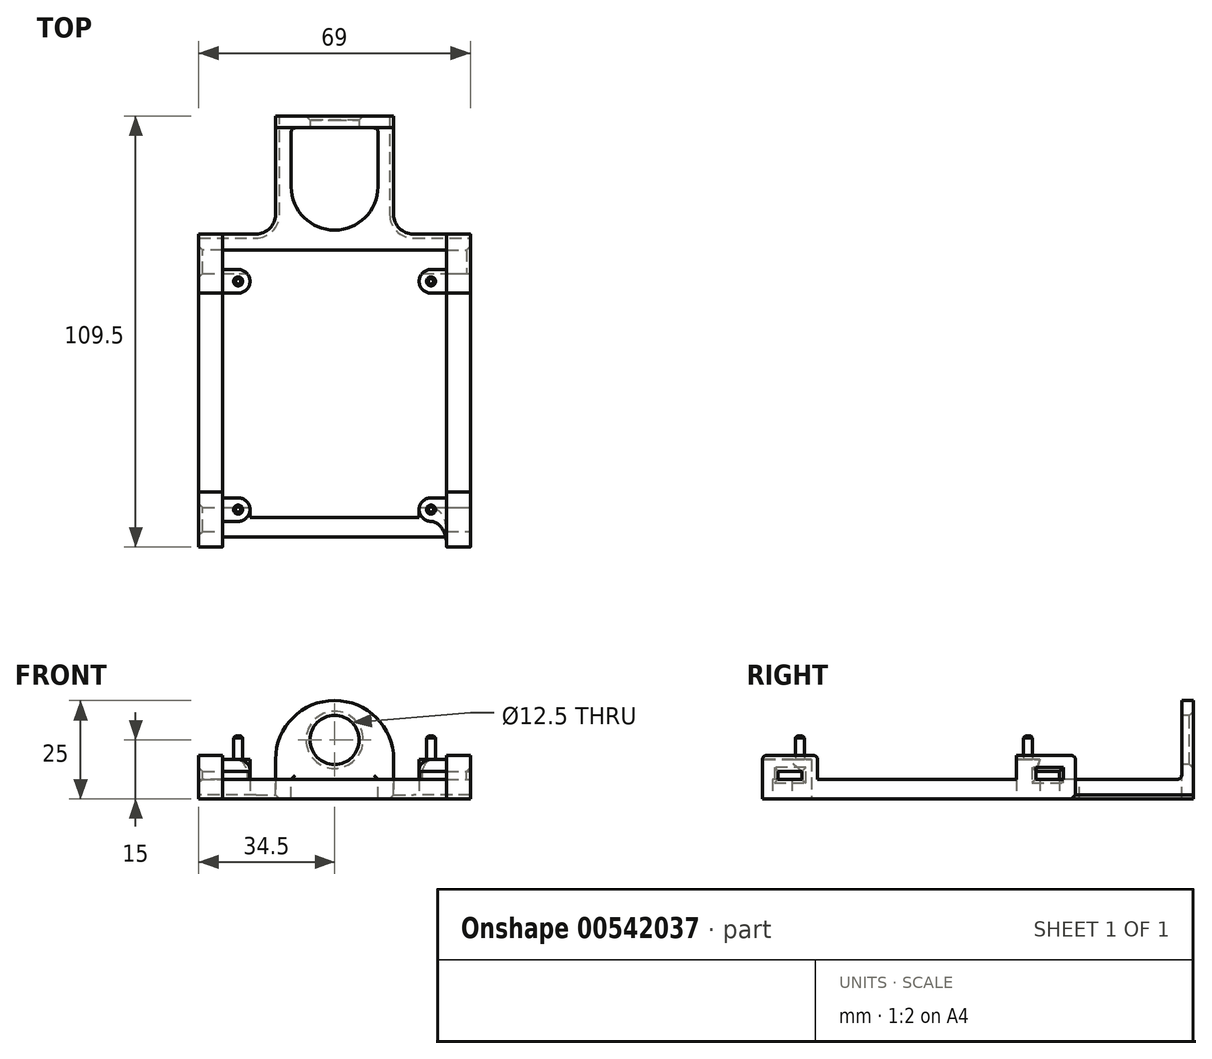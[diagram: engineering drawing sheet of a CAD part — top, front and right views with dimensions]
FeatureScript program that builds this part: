
annotation { "Feature Type Name" : "Feature", "Feature Type Description" : "" }
export const myFeature = defineFeature(function(context is Context, id is Id, definition is map)
    precondition{}
    {
        {
            var Q0;
            Q0=qCreatedBy(makeId("Top.planeOp"),FACE);
            var sketch = newSketch(context, id + "F0", { "sketchPlane" : qUnion([Q0])});
            skCircle(sketch, "E0", {"center": v(0, 58) * mm, "radius": 3 * mm, "construction": true});
            skCircle(sketch, "E1", {"center": v(49, 58) * mm, "radius": 3 * mm, "construction": true});
            skCircle(sketch, "E2", {"center": v(0, 0) * mm, "radius": 3 * mm, "construction": true});
            skCircle(sketch, "E3", {"center": v(49, 0) * mm, "radius": 3 * mm, "construction": true});
            skLineSegment(sketch, "E4", {"start": v(0, 58) * mm, "end": v(0, 0) * mm, "construction": true});
            skLineSegment(sketch, "E5", {"start": v(49, 0) * mm, "end": v(49, 58) * mm, "construction": true});
            skLineSegment(sketch, "E6", {"start": v(0, 58) * mm, "end": v(49, 58) * mm, "construction": true});
            skLineSegment(sketch, "E7", {"start": v(49, 0) * mm, "end": v(0, 0) * mm, "construction": true});
            skLineSegment(sketch, "E8", {"start": v(53, 87) * mm, "end": v(59, 87) * mm});
            skLineSegment(sketch, "E9", {"start": v(59, 87) * mm, "end": v(59, -8) * mm});
            skLineSegment(sketch, "E10", {"start": v(59, -8) * mm, "end": v(-10, -8) * mm});
            skLineSegment(sketch, "E11", {"start": v(-10, -8) * mm, "end": v(-10, 87) * mm});
            skLineSegment(sketch, "E12", {"start": v(-10, 87) * mm, "end": v(-4, 87) * mm});
            skLineSegment(sketch, "E13", {"start": v(-4, -2) * mm, "end": v(53, -2) * mm});
            skLineSegment(sketch, "E14", {"start": v(-4, 61) * mm, "end": v(0, 61) * mm});
            skLineSegment(sketch, "E15", {"start": v(0, 55) * mm, "end": v(-4, 55) * mm});
            skLineSegment(sketch, "E16", {"start": v(-4, 87) * mm, "end": v(-4, 61) * mm});
            skLineSegment(sketch, "E17", {"start": v(-4, 55) * mm, "end": v(-4, -2) * mm});
            skLineSegment(sketch, "E18", {"start": v(49, 55) * mm, "end": v(53, 55) * mm});
            skArc(sketch, "E19", {"start": v(49, 61) * mm, "mid": v(46, 58) * mm, "end": v(49, 55) * mm});
            skLineSegment(sketch, "E20", {"start": v(53, 87) * mm, "end": v(53, 61) * mm});
            skLineSegment(sketch, "E21", {"start": v(53, 55) * mm, "end": v(53, -2) * mm});
            skLineSegment(sketch, "E22", {"start": v(49, 61) * mm, "end": v(53, 61) * mm});
            skArc(sketch, "E23", {"start": v(0, 55) * mm, "mid": v(3, 58) * mm, "end": v(0, 61) * mm});
            skSolve(sketch);
        }
        {
            var Q0;
            Q0=qSketchRegion(id+"F0",true);
            extrude(context, id + "F1", {"entities" : qUnion([Q0]), "depth" : 5 * mm, "offsetDistance" : 25 * mm});
        }
        {
            var Q0;
            Q0=makeQuery(id+"F0.imprint","IMPRINT",FACE,{"disambiguationData":[TD([[makeQuery(id+"F0.imprint","IMPRINT",EDGE,{"derivedFrom":sQuery(id+"F0.wireOp",EDGE,"E8")}),-1.0]])]});
            var sketch = newSketch(context, id + "F2", { "sketchPlane" : qUnion([Q0])});
            skCircle(sketch, "E24.0", {"center": v(0, 0) * mm, "radius": 3 * mm});
            skCircle(sketch, "E24.1", {"center": v(49, 0) * mm, "radius": 3 * mm});
            skCircle(sketch, "E24.2", {"center": v(49, 58) * mm, "radius": 3 * mm});
            skCircle(sketch, "E24.3", {"center": v(0, 58) * mm, "radius": 3 * mm});
            skSolve(sketch);
        }
        {
            var Q0;
            {var subQ0=sQuery(id+"F2.wireOp",EDGE,"E24.0");var subQ1=makeQuery(id+"F0.imprint","IMPRINT",EDGE,{"derivedFrom":sQuery(id+"F0.wireOp",EDGE,"z0m1eTGF-zZ5E-Jgir-b5gq-jupZHO1aANQM")});var subQ2=makeQuery(id+"F2.imprint","INTERSECT",VERTEX,{"disambiguationData":[OD(0.0)],"derivedFrom":[subQ1,subQ0]});Q0=makeQuery(id+"F2.imprint","IMPRINT",FACE,{"disambiguationData":[TD([[makeQuery(id+"F2.imprint","IMPRINT",EDGE,{"disambiguationData":[TD([[subQ2,-1.0]])],"derivedFrom":subQ0}),1.0]])]});}
            var Q1;
            {var subQ0=sQuery(id+"F2.wireOp",EDGE,"E24.1");var subQ1=makeQuery(id+"F0.imprint","IMPRINT",EDGE,{"derivedFrom":sQuery(id+"F0.wireOp",EDGE,"CqdVWxwD-0q4v-9Kh3-cIFh-dPhWwpQpFwKd")});var subQ2=makeQuery(id+"F2.imprint","INTERSECT",VERTEX,{"disambiguationData":[OD(0.0)],"derivedFrom":[subQ1,subQ0]});Q1=makeQuery(id+"F2.imprint","IMPRINT",FACE,{"disambiguationData":[TD([[makeQuery(id+"F2.imprint","IMPRINT",EDGE,{"disambiguationData":[TD([[subQ2,1.0]])],"derivedFrom":subQ0}),1.0]])]});}
            var Q2;
            {var subQ0=sQuery(id+"F2.wireOp",EDGE,"E24.2");var subQ1=makeQuery(id+"F0.imprint","IMPRINT",EDGE,{"derivedFrom":sQuery(id+"F0.wireOp",EDGE,"CqdVWxwD-0q4v-9Kh3-cIFh-dPhWwpQpFwKd")});var subQ2=makeQuery(id+"F2.imprint","INTERSECT",VERTEX,{"disambiguationData":[OD(0.0)],"derivedFrom":[subQ1,subQ0]});Q2=makeQuery(id+"F2.imprint","IMPRINT",FACE,{"disambiguationData":[TD([[makeQuery(id+"F2.imprint","IMPRINT",EDGE,{"disambiguationData":[TD([[subQ2,-1.0]])],"derivedFrom":subQ0}),1.0]])]});}
            var Q3;
            {var subQ0=sQuery(id+"F2.wireOp",EDGE,"E24.3");var subQ1=makeQuery(id+"F0.imprint","IMPRINT",EDGE,{"derivedFrom":sQuery(id+"F0.wireOp",EDGE,"z0m1eTGF-zZ5E-Jgir-b5gq-jupZHO1aANQM")});var subQ2=makeQuery(id+"F2.imprint","INTERSECT",VERTEX,{"disambiguationData":[OD(0.0)],"derivedFrom":[subQ1,subQ0]});Q3=makeQuery(id+"F2.imprint","IMPRINT",FACE,{"disambiguationData":[TD([[makeQuery(id+"F2.imprint","IMPRINT",EDGE,{"disambiguationData":[TD([[subQ2,1.0]])],"derivedFrom":subQ0}),1.0]])]});}
            var Q4;
            {var subQ0=sQuery(id+"F2.wireOp",EDGE,"E24.0");var subQ1=makeQuery(id+"F0.imprint","IMPRINT",EDGE,{"derivedFrom":sQuery(id+"F0.wireOp",EDGE,"z0m1eTGF-zZ5E-Jgir-b5gq-jupZHO1aANQM")});var subQ2=makeQuery(id+"F2.imprint","INTERSECT",VERTEX,{"disambiguationData":[OD(0.0)],"derivedFrom":[subQ1,subQ0]});Q4=makeQuery(id+"F2.imprint","IMPRINT",FACE,{"disambiguationData":[TD([[makeQuery(id+"F2.imprint","IMPRINT",EDGE,{"disambiguationData":[TD([[subQ2,1.0]])],"derivedFrom":subQ0}),1.0]])]});}
            var Q5;
            {var subQ0=sQuery(id+"F2.wireOp",EDGE,"E24.1");var subQ1=makeQuery(id+"F0.imprint","IMPRINT",EDGE,{"derivedFrom":sQuery(id+"F0.wireOp",EDGE,"CqdVWxwD-0q4v-9Kh3-cIFh-dPhWwpQpFwKd")});var subQ2=makeQuery(id+"F2.imprint","INTERSECT",VERTEX,{"disambiguationData":[OD(0.0)],"derivedFrom":[subQ1,subQ0]});Q5=makeQuery(id+"F2.imprint","IMPRINT",FACE,{"disambiguationData":[TD([[makeQuery(id+"F2.imprint","IMPRINT",EDGE,{"disambiguationData":[TD([[subQ2,-1.0]])],"derivedFrom":subQ0}),1.0]])]});}
            var Q6;
            {var subQ0=sQuery(id+"F2.wireOp",EDGE,"E24.2");var subQ1=makeQuery(id+"F0.imprint","IMPRINT",EDGE,{"derivedFrom":sQuery(id+"F0.wireOp",EDGE,"CqdVWxwD-0q4v-9Kh3-cIFh-dPhWwpQpFwKd")});var subQ2=makeQuery(id+"F2.imprint","INTERSECT",VERTEX,{"disambiguationData":[OD(0.0)],"derivedFrom":[subQ1,subQ0]});Q6=makeQuery(id+"F2.imprint","IMPRINT",FACE,{"disambiguationData":[TD([[makeQuery(id+"F2.imprint","IMPRINT",EDGE,{"disambiguationData":[TD([[subQ2,1.0]])],"derivedFrom":subQ0}),1.0]])]});}
            var Q7;
            {var subQ0=sQuery(id+"F2.wireOp",EDGE,"E24.3");var subQ1=makeQuery(id+"F0.imprint","IMPRINT",EDGE,{"derivedFrom":sQuery(id+"F0.wireOp",EDGE,"z0m1eTGF-zZ5E-Jgir-b5gq-jupZHO1aANQM")});var subQ2=makeQuery(id+"F2.imprint","INTERSECT",VERTEX,{"disambiguationData":[OD(0.0)],"derivedFrom":[subQ1,subQ0]});Q7=makeQuery(id+"F2.imprint","IMPRINT",FACE,{"disambiguationData":[TD([[makeQuery(id+"F2.imprint","IMPRINT",EDGE,{"disambiguationData":[TD([[subQ2,-1.0]])],"derivedFrom":subQ0}),1.0]])]});}
            extrude(context, id + "F3", {"entities" : qUnion([Q0, Q1, Q2, Q3, Q4, Q5, Q6, Q7]), "operationType" : NewBodyOperationType.ADD, "depth" : 10 * mm, "offsetDistance" : 25 * mm});
        }
        {
            var Q0;
            Q0=makeQuery(id+"F3.opExtrude","CAP_FACE",FACE,{"disambiguationData":[OSD([sQuery(id+"F2.wireOp",EDGE,"E24.3")])],"isStart":false});
            var sketch = newSketch(context, id + "F4", { "sketchPlane" : qUnion([Q0])});
            skCircle(sketch, "E25", {"center": v(0, 58) * mm, "radius": 1.15 * mm});
            skCircle(sketch, "E26", {"center": v(49, 58) * mm, "radius": 1.15 * mm});
            skCircle(sketch, "E27", {"center": v(49, 0) * mm, "radius": 1.15 * mm});
            skCircle(sketch, "E28", {"center": v(0, 0) * mm, "radius": 1.15 * mm});
            skSolve(sketch);
        }
        {
            var Q0;
            Q0=qSketchRegion(id+"F4",true);
            extrude(context, id + "F5", {"entities" : qUnion([Q0]), "operationType" : NewBodyOperationType.ADD, "depth" : 6 * mm, "offsetDistance" : 25 * mm});
        }
        {
            var Q0;
            Q0=makeQuery(id+"F5.opExtrude","CAP_EDGE",EDGE,{"disambiguationData":[OSD([sQuery(id+"F4.wireOp",EDGE,"E25")])],"isStart":false});
            var Q1;
            Q1=makeQuery(id+"F5.opExtrude","CAP_EDGE",EDGE,{"disambiguationData":[OSD([sQuery(id+"F4.wireOp",EDGE,"E26")])],"isStart":false});
            var Q2;
            Q2=makeQuery(id+"F5.opExtrude","CAP_EDGE",EDGE,{"disambiguationData":[OSD([sQuery(id+"F4.wireOp",EDGE,"E27")])],"isStart":false});
            var Q3;
            Q3=makeQuery(id+"F5.opExtrude","CAP_EDGE",EDGE,{"disambiguationData":[OSD([sQuery(id+"F4.wireOp",EDGE,"E28")])],"isStart":false});
            chamfer(context, id + "F6", {"entities" : qUnion([Q0, Q1, Q2, Q3]), "width" : 0.5 * mm, "tangentPropagation" : true});
        }
        {
            var Q0;
            Q0=makeQuery(id+"F0.imprint","IMPRINT",FACE,{"disambiguationData":[TD([[makeQuery(id+"F0.imprint","IMPRINT",EDGE,{"derivedFrom":sQuery(id+"F0.wireOp",EDGE,"E8")}),-1.0]])]});
            var sketch = newSketch(context, id + "F7", { "sketchPlane" : qUnion([Q0])});
            skLineSegment(sketch, "E29", {"start": v(53, 3) * mm, "end": v(49, 3) * mm});
            skLineSegment(sketch, "E30", {"start": v(49, 3) * mm, "end": v(49, 0) * mm});
            skLineSegment(sketch, "E31", {"start": v(49, 0) * mm, "end": v(46, 0) * mm});
            skLineSegment(sketch, "E32", {"start": v(46, 0) * mm, "end": v(46, -2) * mm});
            skLineSegment(sketch, "E33", {"start": v(46, -2) * mm, "end": v(53, -2) * mm});
            skLineSegment(sketch, "E34", {"start": v(53, -2) * mm, "end": v(53, 3) * mm});
            skLineSegment(sketch, "E35", {"start": v(3, -2) * mm, "end": v(3, 0) * mm});
            skLineSegment(sketch, "E36", {"start": v(3, 0) * mm, "end": v(0, 0) * mm});
            skLineSegment(sketch, "E37", {"start": v(0, 0) * mm, "end": v(0, 3) * mm});
            skLineSegment(sketch, "E38", {"start": v(0, 3) * mm, "end": v(-4, 3) * mm});
            skLineSegment(sketch, "E39", {"start": v(-4, 3) * mm, "end": v(-4, -2) * mm});
            skLineSegment(sketch, "E40", {"start": v(-4, -2) * mm, "end": v(3, -2) * mm});
            skSolve(sketch);
        }
        {
            var Q0;
            Q0=qSketchRegion(id+"F7",true);
            var Q1;
            Q1=makeQuery(id+"F1.opExtrude","CAP_FACE",FACE,{"disambiguationData":[OSD([sQuery(id+"F0.wireOp",EDGE,"E8"),sQuery(id+"F0.wireOp",EDGE,"E9"),sQuery(id+"F0.wireOp",EDGE,"E10"),sQuery(id+"F0.wireOp",EDGE,"E11"),sQuery(id+"F0.wireOp",EDGE,"E12"),sQuery(id+"F0.wireOp",EDGE,"E13"),sQuery(id+"F0.wireOp",EDGE,"E14"),sQuery(id+"F0.wireOp",EDGE,"E15"),sQuery(id+"F0.wireOp",EDGE,"E16"),sQuery(id+"F0.wireOp",EDGE,"E17"),sQuery(id+"F0.wireOp",EDGE,"E18"),sQuery(id+"F0.wireOp",EDGE,"E19"),sQuery(id+"F0.wireOp",EDGE,"E20"),sQuery(id+"F0.wireOp",EDGE,"E21"),sQuery(id+"F0.wireOp",EDGE,"E22"),sQuery(id+"F0.wireOp",EDGE,"E23")])],"isStart":false});
            extrude(context, id + "F8", {"entities" : qUnion([Q0]), "operationType" : NewBodyOperationType.ADD, "endBound" : BoundingType.UP_TO_SURFACE, "depth" : 25 * mm, "endBoundEntityFace" : qUnion([Q1]), "offsetDistance" : 25 * mm});
        }
        {
            var Q0;
            {var subQ0=sQuery(id+"F0.wireOp",EDGE,"E23");var subQ1=sQuery(id+"F0.wireOp",EDGE,"E22");var subQ2=sQuery(id+"F0.wireOp",EDGE,"E21");var subQ3=sQuery(id+"F0.wireOp",EDGE,"E20");var subQ4=sQuery(id+"F0.wireOp",EDGE,"E19");var subQ5=sQuery(id+"F0.wireOp",EDGE,"E18");var subQ6=sQuery(id+"F0.wireOp",EDGE,"E17");var subQ7=sQuery(id+"F0.wireOp",EDGE,"E16");var subQ8=sQuery(id+"F0.wireOp",EDGE,"E15");var subQ9=sQuery(id+"F0.wireOp",EDGE,"E14");var subQ10=sQuery(id+"F0.wireOp",EDGE,"E13");var subQ11=sQuery(id+"F0.wireOp",EDGE,"E12");var subQ12=sQuery(id+"F0.wireOp",EDGE,"E11");var subQ13=sQuery(id+"F0.wireOp",EDGE,"E10");var subQ14=sQuery(id+"F0.wireOp",EDGE,"E9");var subQ15=sQuery(id+"F0.wireOp",EDGE,"E8");Q0=makeQuery(id+"F8.boolean.opBoolean","MERGE",FACE,{"derivedFrom":[makeQuery(id+"F1.opExtrude","CAP_FACE",FACE,{"disambiguationData":[OSD([subQ15,subQ14,subQ13,subQ12,subQ11,subQ10,subQ9,subQ8,subQ7,subQ6,subQ5,subQ4,subQ3,subQ2,subQ1,subQ0])],"isStart":false}),makeQuery(id+"F8.opExtrude","CAP_FACE",FACE,{"disambiguationData":[OSD([subQ15,subQ14,subQ13,subQ12,subQ11,subQ10,subQ9,subQ8,subQ7,subQ6,subQ5,subQ4,subQ3,subQ2,subQ1,subQ0]),OD(0.0)],"isStart":false}),makeQuery(id+"F8.opExtrude","CAP_FACE",FACE,{"disambiguationData":[OSD([subQ15,subQ14,subQ13,subQ12,subQ11,subQ10,subQ9,subQ8,subQ7,subQ6,subQ5,subQ4,subQ3,subQ2,subQ1,subQ0]),OD(1.0)],"isStart":false})]});}
            var sketch = newSketch(context, id + "F9", { "sketchPlane" : qUnion([Q0])});
            skLineSegment(sketch, "E41.0", {"start": v(0, 3) * mm, "end": v(-4, 3) * mm});
            skLineSegment(sketch, "E42", {"start": v(0, -3) * mm, "end": v(-10, -3) * mm});
            skLineSegment(sketch, "E43", {"start": v(-10, -3) * mm, "end": v(-10, 3) * mm});
            skLineSegment(sketch, "E44", {"start": v(-10, 3) * mm, "end": v(-4, 3) * mm});
            skArc(sketch, "E45", {"start": v(0, 3) * mm, "mid": v(-3, 0) * mm, "end": v(0, -3) * mm});
            skLineSegment(sketch, "E46.0", {"start": v(53, 3) * mm, "end": v(49, 3) * mm});
            skLineSegment(sketch, "E47", {"start": v(53, 3) * mm, "end": v(59, 3) * mm});
            skLineSegment(sketch, "E48", {"start": v(49, -3) * mm, "end": v(59, -3) * mm});
            skLineSegment(sketch, "E49", {"start": v(59, -3) * mm, "end": v(59, 3) * mm});
            skArc(sketch, "E50", {"start": v(49, -3) * mm, "mid": v(52, 0) * mm, "end": v(49, 3) * mm});
            skArc(sketch, "E51.0", {"start": v(49, 61) * mm, "mid": v(52, 58) * mm, "end": v(49, 55) * mm});
            skLineSegment(sketch, "E51.1", {"start": v(49, 61) * mm, "end": v(53, 61) * mm});
            skLineSegment(sketch, "E51.2", {"start": v(49, 55) * mm, "end": v(53, 55) * mm});
            skLineSegment(sketch, "E52", {"start": v(53, 55) * mm, "end": v(59, 55) * mm});
            skLineSegment(sketch, "E53", {"start": v(59, 55) * mm, "end": v(59, 61) * mm});
            skLineSegment(sketch, "E54", {"start": v(59, 61) * mm, "end": v(53, 61) * mm});
            skArc(sketch, "E55.0", {"start": v(0, 55) * mm, "mid": v(-3, 58) * mm, "end": v(0, 61) * mm});
            skLineSegment(sketch, "E56.0", {"start": v(-4, 61) * mm, "end": v(0, 61) * mm});
            skLineSegment(sketch, "E56.1", {"start": v(0, 55) * mm, "end": v(-4, 55) * mm});
            skLineSegment(sketch, "E57", {"start": v(-4, 61) * mm, "end": v(-10, 61) * mm});
            skLineSegment(sketch, "E58", {"start": v(-10, 61) * mm, "end": v(-10, 55) * mm});
            skLineSegment(sketch, "E59", {"start": v(-10, 55) * mm, "end": v(-4, 55) * mm});
            skSolve(sketch);
        }
        {
            var Q0;
            Q0 = qSketchRegion(id + "F9", true);
            var Q1;
            Q1=makeQuery(id+"F3.opExtrude","CAP_FACE",FACE,{"disambiguationData":[OSD([sQuery(id+"F2.wireOp",EDGE,"E24.0")])],"isStart":false});
            extrude(context, id + "F10", {"entities" : qUnion([Q0]), "operationType" : NewBodyOperationType.ADD, "endBound" : BoundingType.UP_TO_SURFACE, "depth" : 25 * mm, "endBoundEntityFace" : qUnion([Q1]), "offsetDistance" : 25 * mm});
        }
        {
            var Q0;
            {var subQ2=sQuery(id+"F0.wireOp",EDGE,"E10");var subQ3=sQuery(id+"F0.wireOp",EDGE,"E9");var subQ5=sQuery(id+"F0.wireOp",EDGE,"E13");var subQ6=sQuery(id+"F0.wireOp",EDGE,"E11");var subQ10=sQuery(id+"F0.wireOp",EDGE,"E23");var subQ11=sQuery(id+"F0.wireOp",EDGE,"E22");var subQ12=sQuery(id+"F0.wireOp",EDGE,"E21");var subQ13=sQuery(id+"F0.wireOp",EDGE,"E20");var subQ14=sQuery(id+"F0.wireOp",EDGE,"E19");var subQ15=sQuery(id+"F0.wireOp",EDGE,"E18");var subQ16=sQuery(id+"F0.wireOp",EDGE,"E17");var subQ17=sQuery(id+"F0.wireOp",EDGE,"E16");var subQ18=sQuery(id+"F0.wireOp",EDGE,"E15");var subQ19=sQuery(id+"F0.wireOp",EDGE,"E14");var subQ20=sQuery(id+"F0.wireOp",EDGE,"E12");var subQ21=sQuery(id+"F0.wireOp",EDGE,"E8");var subQ22=makeQuery(id+"F8.boolean.opBoolean","MERGE",FACE,{"derivedFrom":[makeQuery(id+"F1.opExtrude","CAP_FACE",FACE,{"disambiguationData":[OSD([subQ21,subQ3,subQ2,subQ6,subQ20,subQ5,subQ19,subQ18,subQ17,subQ16,subQ15,subQ14,subQ13,subQ12,subQ11,subQ10])],"isStart":false}),makeQuery(id+"F8.opExtrude","CAP_FACE",FACE,{"disambiguationData":[OSD([subQ21,subQ3,subQ2,subQ6,subQ20,subQ5,subQ19,subQ18,subQ17,subQ16,subQ15,subQ14,subQ13,subQ12,subQ11,subQ10]),OD(0.0)],"isStart":false}),makeQuery(id+"F8.opExtrude","CAP_FACE",FACE,{"disambiguationData":[OSD([subQ21,subQ3,subQ2,subQ6,subQ20,subQ5,subQ19,subQ18,subQ17,subQ16,subQ15,subQ14,subQ13,subQ12,subQ11,subQ10]),OD(1.0)],"isStart":false})]});Q0=makeQuery(id+"FzJLuCjRFesb7Eh_1.boolean.opBoolean","MERGE",FACE,{"derivedFrom":[makeQuery(id+"F10.boolean.opBoolean","SPLIT",FACE,{"disambiguationData":[TD([makeQuery(id+"F1.opExtrude","SWEPT_FACE",FACE,{"disambiguationData":[OSD([subQ21])]})])],"derivedFrom":subQ22}),makeQuery(id+"F10.boolean.opBoolean","SPLIT",FACE,{"disambiguationData":[TD([makeQuery(id+"F1.opExtrude","SWEPT_FACE",FACE,{"disambiguationData":[OSD([subQ20])]})])],"derivedFrom":subQ22}),makeQuery(id+"F10.boolean.opBoolean","SPLIT",FACE,{"disambiguationData":[TD([makeQuery(id+"F1.opExtrude","SWEPT_FACE",FACE,{"disambiguationData":[OSD([subQ18])]})])],"derivedFrom":subQ22}),makeQuery(id+"F10.boolean.opBoolean","SPLIT",FACE,{"disambiguationData":[TD([makeQuery(id+"F1.opExtrude","SWEPT_FACE",FACE,{"disambiguationData":[OSD([subQ15])]})])],"derivedFrom":subQ22}),makeQuery(id+"F10.boolean.opBoolean","SPLIT",FACE,{"disambiguationData":[TD([makeQuery(id+"F1.opExtrude","SWEPT_FACE",FACE,{"disambiguationData":[OSD([subQ2])]})])],"derivedFrom":subQ22}),makeQuery(id+"FzJLuCjRFesb7Eh_1.opExtrude","SWEPT_FACE",FACE,{"disambiguationData":[OSD([sQuery(id+"FK3UFjTJBH50bIp_1.wireOp",EDGE,"B9w6mIKw-4OBh-PMY4-QLSO-k9XiWoAq1MY0")])]}),makeQuery(id+"FzJLuCjRFesb7Eh_1.opExtrude","SWEPT_FACE",FACE,{"disambiguationData":[OSD([sQuery(id+"FK3UFjTJBH50bIp_1.wireOp",EDGE,"2909b156-10ae-4258-a5fb-6503340ec8435.MirrorCS")])]})]});}
            var sketch = newSketch(context, id + "F11", { "sketchPlane" : qUnion([Q0])});
            skLineSegment(sketch, "E60", {"start": v(53, 94) * mm, "end": v(-4, 94) * mm});
            skLineSegment(sketch, "E61", {"start": v(24.5, 94) * mm, "end": v(24.5, 58) * mm, "construction": true});
            skLineSegment(sketch, "E62", {"start": v(-10, 100) * mm, "end": v(59, 100) * mm});
            skLineSegment(sketch, "E63", {"start": v(24.5, 94) * mm, "end": v(24.5, 100) * mm, "construction": true});
            skLineSegment(sketch, "E64", {"start": v(-10, 87) * mm, "end": v(-4, 87) * mm});
            skLineSegment(sketch, "E65", {"start": v(53, 87) * mm, "end": v(59, 87) * mm});
            skPoint(sketch, "E66.visualSharp", {"position": v(7.57, 74.85) * mm});
            skPoint(sketch, "E67.visualSharp", {"position": v(13.57, 74.85) * mm});
            skPoint(sketch, "E68.visualSharp", {"position": v(35.43, 99.85) * mm});
            skPoint(sketch, "E69.visualSharp", {"position": v(41.43, 74.85) * mm});
            skLineSegment(sketch, "E70", {"start": v(59, 87) * mm, "end": v(59, 100) * mm});
            skLineSegment(sketch, "E71", {"start": v(53, 94) * mm, "end": v(53, 87) * mm});
            skLineSegment(sketch, "E72", {"start": v(-4, 87) * mm, "end": v(-4, 94) * mm});
            skLineSegment(sketch, "E73", {"start": v(-10, 100) * mm, "end": v(-10, 87) * mm});
            skSolve(sketch);
        }
        {
            var Q0;
            Q0=makeQuery(id+"F11.imprint","IMPRINT",FACE,{"disambiguationData":[TD([[makeQuery(id+"F11.imprint","IMPRINT",EDGE,{"derivedFrom":sQuery(id+"F11.wireOp",EDGE,"E60")}),-1.0]])]});
            var Q1;
            Q1=makeQuery(id+"F8.boolean.opBoolean","MERGE",FACE,{"derivedFrom":[makeQuery(id+"F3.boolean.opBoolean","MERGE",FACE,{"derivedFrom":[makeQuery(id+"F1.opExtrude","CAP_FACE",FACE,{"disambiguationData":[OSD([sQuery(id+"F0.wireOp",EDGE,"E8"),sQuery(id+"F0.wireOp",EDGE,"E9"),sQuery(id+"F0.wireOp",EDGE,"E10"),sQuery(id+"F0.wireOp",EDGE,"E11"),sQuery(id+"F0.wireOp",EDGE,"E12"),sQuery(id+"F0.wireOp",EDGE,"E13"),sQuery(id+"F0.wireOp",EDGE,"E14"),sQuery(id+"F0.wireOp",EDGE,"E15"),sQuery(id+"F0.wireOp",EDGE,"E16"),sQuery(id+"F0.wireOp",EDGE,"E17"),sQuery(id+"F0.wireOp",EDGE,"E18"),sQuery(id+"F0.wireOp",EDGE,"E19"),sQuery(id+"F0.wireOp",EDGE,"E20"),sQuery(id+"F0.wireOp",EDGE,"E21"),sQuery(id+"F0.wireOp",EDGE,"E22"),sQuery(id+"F0.wireOp",EDGE,"E23")])],"isStart":true}),makeQuery(id+"F3.opExtrude","CAP_FACE",FACE,{"disambiguationData":[OSD([sQuery(id+"F2.wireOp",EDGE,"E24.0")])],"isStart":true}),makeQuery(id+"F3.opExtrude","CAP_FACE",FACE,{"disambiguationData":[OSD([sQuery(id+"F2.wireOp",EDGE,"E24.1")])],"isStart":true})]}),makeQuery(id+"F8.opExtrude","CAP_FACE",FACE,{"disambiguationData":[OSD([sQuery(id+"F7.wireOp",EDGE,"E29"),sQuery(id+"F7.wireOp",EDGE,"E30"),sQuery(id+"F7.wireOp",EDGE,"E31"),sQuery(id+"F7.wireOp",EDGE,"E32"),sQuery(id+"F7.wireOp",EDGE,"E33"),sQuery(id+"F7.wireOp",EDGE,"E34")])],"isStart":true}),makeQuery(id+"F8.opExtrude","CAP_FACE",FACE,{"disambiguationData":[OSD([sQuery(id+"F7.wireOp",EDGE,"E35"),sQuery(id+"F7.wireOp",EDGE,"E36"),sQuery(id+"F7.wireOp",EDGE,"E37"),sQuery(id+"F7.wireOp",EDGE,"E38"),sQuery(id+"F7.wireOp",EDGE,"E39"),sQuery(id+"F7.wireOp",EDGE,"E40")])],"isStart":true})]});
            extrude(context, id + "F12", {"entities" : qUnion([Q0]), "operationType" : NewBodyOperationType.ADD, "endBound" : BoundingType.UP_TO_SURFACE, "oppositeDirection" : true, "depth" : 25 * mm, "endBoundEntityFace" : qUnion([Q1]), "offsetDistance" : 25 * mm});
        }
        {
            var Q0;
            {var subQ2=sQuery(id+"F0.wireOp",EDGE,"E10");var subQ3=sQuery(id+"F0.wireOp",EDGE,"E9");var subQ5=sQuery(id+"F0.wireOp",EDGE,"E13");var subQ6=sQuery(id+"F0.wireOp",EDGE,"E11");var subQ10=sQuery(id+"F0.wireOp",EDGE,"E23");var subQ11=sQuery(id+"F0.wireOp",EDGE,"E22");var subQ12=sQuery(id+"F0.wireOp",EDGE,"E21");var subQ13=sQuery(id+"F0.wireOp",EDGE,"E20");var subQ14=sQuery(id+"F0.wireOp",EDGE,"E19");var subQ15=sQuery(id+"F0.wireOp",EDGE,"E18");var subQ16=sQuery(id+"F0.wireOp",EDGE,"E17");var subQ17=sQuery(id+"F0.wireOp",EDGE,"E16");var subQ18=sQuery(id+"F0.wireOp",EDGE,"E15");var subQ19=sQuery(id+"F0.wireOp",EDGE,"E14");var subQ20=sQuery(id+"F0.wireOp",EDGE,"E12");var subQ21=sQuery(id+"F0.wireOp",EDGE,"E8");var subQ22=makeQuery(id+"F8.boolean.opBoolean","MERGE",FACE,{"derivedFrom":[makeQuery(id+"F1.opExtrude","CAP_FACE",FACE,{"disambiguationData":[OSD([subQ21,subQ3,subQ2,subQ6,subQ20,subQ5,subQ19,subQ18,subQ17,subQ16,subQ15,subQ14,subQ13,subQ12,subQ11,subQ10])],"isStart":false}),makeQuery(id+"F8.opExtrude","CAP_FACE",FACE,{"disambiguationData":[OSD([subQ21,subQ3,subQ2,subQ6,subQ20,subQ5,subQ19,subQ18,subQ17,subQ16,subQ15,subQ14,subQ13,subQ12,subQ11,subQ10]),OD(0.0)],"isStart":false}),makeQuery(id+"F8.opExtrude","CAP_FACE",FACE,{"disambiguationData":[OSD([subQ21,subQ3,subQ2,subQ6,subQ20,subQ5,subQ19,subQ18,subQ17,subQ16,subQ15,subQ14,subQ13,subQ12,subQ11,subQ10]),OD(1.0)],"isStart":false})]});Q0=makeQuery(id+"F12.boolean.opBoolean","MERGE",FACE,{"derivedFrom":[makeQuery(id+"FzJLuCjRFesb7Eh_1.boolean.opBoolean","MERGE",FACE,{"derivedFrom":[makeQuery(id+"F10.boolean.opBoolean","SPLIT",FACE,{"disambiguationData":[TD([makeQuery(id+"F1.opExtrude","SWEPT_FACE",FACE,{"disambiguationData":[OSD([subQ21])]})])],"derivedFrom":subQ22}),makeQuery(id+"F10.boolean.opBoolean","SPLIT",FACE,{"disambiguationData":[TD([makeQuery(id+"F1.opExtrude","SWEPT_FACE",FACE,{"disambiguationData":[OSD([subQ20])]})])],"derivedFrom":subQ22}),makeQuery(id+"F10.boolean.opBoolean","SPLIT",FACE,{"disambiguationData":[TD([makeQuery(id+"F1.opExtrude","SWEPT_FACE",FACE,{"disambiguationData":[OSD([subQ18])]})])],"derivedFrom":subQ22}),makeQuery(id+"F10.boolean.opBoolean","SPLIT",FACE,{"disambiguationData":[TD([makeQuery(id+"F1.opExtrude","SWEPT_FACE",FACE,{"disambiguationData":[OSD([subQ15])]})])],"derivedFrom":subQ22}),makeQuery(id+"F10.boolean.opBoolean","SPLIT",FACE,{"disambiguationData":[TD([makeQuery(id+"F1.opExtrude","SWEPT_FACE",FACE,{"disambiguationData":[OSD([subQ2])]})])],"derivedFrom":subQ22}),makeQuery(id+"FzJLuCjRFesb7Eh_1.opExtrude","SWEPT_FACE",FACE,{"disambiguationData":[OSD([sQuery(id+"FK3UFjTJBH50bIp_1.wireOp",EDGE,"B9w6mIKw-4OBh-PMY4-QLSO-k9XiWoAq1MY0")])]}),makeQuery(id+"FzJLuCjRFesb7Eh_1.opExtrude","SWEPT_FACE",FACE,{"disambiguationData":[OSD([sQuery(id+"FK3UFjTJBH50bIp_1.wireOp",EDGE,"2909b156-10ae-4258-a5fb-6503340ec8435.MirrorCS")])]})]}),makeQuery(id+"F12.opExtrude","CAP_FACE",FACE,{"disambiguationData":[OSD([sQuery(id+"F11.wireOp",EDGE,"rddHBWp6-PjjR-rAVH-7kwS-blr78lmYVsLx"),sQuery(id+"F11.wireOp",EDGE,"E60"),sQuery(id+"F11.wireOp",EDGE,"kyyKlCdx-T4xm-cmC4-y8FS-BxZtbIvDwNVB"),sQuery(id+"F11.wireOp",EDGE,"9fCqO9sc-L7oK-tlZ9-L6ho-o7iXRhHaUt1G"),sQuery(id+"F11.wireOp",EDGE,"E62"),sQuery(id+"F11.wireOp",EDGE,"reZnIggN-ssMF-izXE-Xq5I-q9KhQ06pSCod"),sQuery(id+"F11.wireOp",EDGE,"E64"),sQuery(id+"F11.wireOp",EDGE,"QFzaI4ww-LD7o-lgD7-kvFv-Lo1Rq7mrhjSk"),sQuery(id+"F11.wireOp",EDGE,"7YUyPcyg-OMKa-eBBQ-sJW8-IEtHnzjoVrz6"),sQuery(id+"F11.wireOp",EDGE,"JmcjC6gf-t5s0-z86i-Iodn-ZretlQtEYflB"),sQuery(id+"F11.wireOp",EDGE,"E65"),sQuery(id+"F11.wireOp",EDGE,"Vvg3P4pu-c9bY-dbKV-2Tf5-B3XEFH06yk6L"),sQuery(id+"F11.wireOp",EDGE,"E66.filletArc"),sQuery(id+"F11.wireOp",EDGE,"E67.filletArc"),sQuery(id+"F11.wireOp",EDGE,"E68.filletArc"),sQuery(id+"F11.wireOp",EDGE,"E69.filletArc")])],"isStart":true})]});}
            var sketch = newSketch(context, id + "F13", { "sketchPlane" : qUnion([Q0])});
            skLineSegment(sketch, "E74.bottom", {"start": v(39.5, 100) * mm, "end": v(9.5, 100) * mm});
            skLineSegment(sketch, "E74.top", {"start": v(39.5, 94) * mm, "end": v(9.5, 94) * mm});
            skLineSegment(sketch, "E74.left", {"start": v(9.5, 100) * mm, "end": v(9.5, 94) * mm});
            skLineSegment(sketch, "E74.right", {"start": v(39.5, 100) * mm, "end": v(39.5, 94) * mm});
            skLineSegment(sketch, "E75", {"start": v(24.5, 94) * mm, "end": v(24.5, 58) * mm, "construction": true});
            skSolve(sketch);
        }
        {
            var Q0;
            Q0 = qSketchRegion(id + "F13", true);
            extrude(context, id + "F14", {"entities" : qUnion([Q0]), "operationType" : NewBodyOperationType.ADD, "depth" : 20 * mm, "offsetDistance" : 25 * mm});
        }
        {
            var Q0;
            Q0=makeQuery(id+"F14.boolean.opBoolean","MERGE",FACE,{"derivedFrom":[makeQuery(id+"F12.opExtrude","SWEPT_FACE",FACE,{"disambiguationData":[OSD([sQuery(id+"F11.wireOp",EDGE,"E60")])]}),makeQuery(id+"F14.opExtrude","SWEPT_FACE",FACE,{"disambiguationData":[OSD([sQuery(id+"F13.wireOp",EDGE,"E74.top")])]})]});
            var sketch = newSketch(context, id + "F15", { "sketchPlane" : qUnion([Q0])});
            skCircle(sketch, "E76", {"center": v(24.5, 15) * mm, "radius": 6.25 * mm});
            skLineSegment(sketch, "E77", {"start": v(24.5, 15) * mm, "end": v(24.5, 25) * mm, "construction": true});
            skLineSegment(sketch, "E78", {"start": v(9.5, 15) * mm, "end": v(24.5, 15) * mm, "construction": true});
            skSolve(sketch);
        }
        {
            var Q0;
            Q0 = qSketchRegion(id + "F15", true);
            extrude(context, id + "F16", {"entities" : qUnion([Q0]), "operationType" : NewBodyOperationType.REMOVE, "oppositeDirection" : true, "depth" : 25 * mm, "offsetDistance" : 25 * mm});
        }
        {
            var Q0;
            Q0=makeQuery(id+"F14.opExtrude","CAP_EDGE",EDGE,{"disambiguationData":[OSD([sQuery(id+"F13.wireOp",EDGE,"E74.right")])],"isStart":false});
            var Q1;
            Q1=makeQuery(id+"F14.opExtrude","CAP_EDGE",EDGE,{"disambiguationData":[OSD([sQuery(id+"F13.wireOp",EDGE,"E74.left")])],"isStart":false});
            fillet(context, id + "F17", {"entities" : qUnion([Q0, Q1]), "radius" : 15 * mm, "tangentPropagation" : true, "allowEdgeOverflow" : false});
        }
        {
            var Q0;
            Q0=makeQuery(id+"F10.boolean.opBoolean","MERGE",FACE,{"derivedFrom":[makeQuery(id+"F3.opExtrude","CAP_FACE",FACE,{"disambiguationData":[OSD([sQuery(id+"F2.wireOp",EDGE,"E24.2")])],"isStart":false}),makeQuery(id+"F10.opExtrude","CAP_FACE",FACE,{"disambiguationData":[OSD([sQuery(id+"F2.wireOp",EDGE,"E24.0")]),OD(2.0)],"isStart":false})]});
            var sketch = newSketch(context, id + "F18", { "sketchPlane" : qUnion([Q0])});
            skLineSegment(sketch, "E79.bottom", {"start": v(59, 61) * mm, "end": v(53, 61) * mm});
            skLineSegment(sketch, "E79.top", {"start": v(59, 65) * mm, "end": v(53, 65) * mm});
            skLineSegment(sketch, "E79.left", {"start": v(59, 61) * mm, "end": v(59, 65) * mm});
            skLineSegment(sketch, "E79.right", {"start": v(53, 61) * mm, "end": v(53, 65) * mm});
            skLineSegment(sketch, "E80.bottom", {"start": v(-10, 61) * mm, "end": v(-4, 61) * mm});
            skLineSegment(sketch, "E80.top", {"start": v(-10, 65) * mm, "end": v(-4, 65) * mm});
            skLineSegment(sketch, "E80.left", {"start": v(-10, 61) * mm, "end": v(-10, 65) * mm});
            skLineSegment(sketch, "E80.right", {"start": v(-4, 61) * mm, "end": v(-4, 65) * mm});
            skLineSegment(sketch, "E81.bottom", {"start": v(59, -3) * mm, "end": v(53, -3) * mm});
            skLineSegment(sketch, "E81.top", {"start": v(59, -8) * mm, "end": v(53, -8) * mm});
            skLineSegment(sketch, "E81.left", {"start": v(59, -3) * mm, "end": v(59, -8) * mm});
            skLineSegment(sketch, "E81.right", {"start": v(53, -3) * mm, "end": v(53, -8) * mm});
            skLineSegment(sketch, "E82.bottom", {"start": v(-10, -8) * mm, "end": v(-4, -8) * mm});
            skLineSegment(sketch, "E82.top", {"start": v(-10, -3) * mm, "end": v(-4, -3) * mm});
            skLineSegment(sketch, "E82.left", {"start": v(-10, -8) * mm, "end": v(-10, -3) * mm});
            skLineSegment(sketch, "E82.right", {"start": v(-4, -8) * mm, "end": v(-4, -3) * mm});
            skSolve(sketch);
        }
        {
            var Q0;
            Q0 = qSketchRegion(id + "F18", true);
            var Q1;
            {var subQ0=sQuery(id+"F11.wireOp",EDGE,"E72");var subQ1=sQuery(id+"F11.wireOp",EDGE,"E62");var subQ3=sQuery(id+"F11.wireOp",EDGE,"E60");var subQ5=sQuery(id+"F0.wireOp",EDGE,"E11");var subQ6=makeQuery(id+"F1.opExtrude","SWEPT_FACE",FACE,{"disambiguationData":[OSD([subQ5])]});var subQ7=sQuery(id+"F11.wireOp",EDGE,"E73");var subQ8=sQuery(id+"F0.wireOp",EDGE,"E16");var subQ10=sQuery(id+"F0.wireOp",EDGE,"E14");var subQ13=sQuery(id+"F0.wireOp",EDGE,"E12");var subQ14=sQuery(id+"F0.wireOp",EDGE,"E23");var subQ15=sQuery(id+"F0.wireOp",EDGE,"E22");var subQ16=sQuery(id+"F0.wireOp",EDGE,"E21");var subQ17=sQuery(id+"F0.wireOp",EDGE,"E20");var subQ18=sQuery(id+"F0.wireOp",EDGE,"E19");var subQ19=sQuery(id+"F0.wireOp",EDGE,"E18");var subQ20=sQuery(id+"F0.wireOp",EDGE,"E17");var subQ21=sQuery(id+"F0.wireOp",EDGE,"E15");var subQ22=sQuery(id+"F0.wireOp",EDGE,"E13");var subQ23=sQuery(id+"F0.wireOp",EDGE,"E10");var subQ24=sQuery(id+"F0.wireOp",EDGE,"E9");var subQ25=sQuery(id+"F0.wireOp",EDGE,"E8");var subQ26=makeQuery(id+"F8.boolean.opBoolean","MERGE",FACE,{"derivedFrom":[makeQuery(id+"F1.opExtrude","CAP_FACE",FACE,{"disambiguationData":[OSD([subQ25,subQ24,subQ23,subQ5,subQ13,subQ22,subQ10,subQ21,subQ8,subQ20,subQ19,subQ18,subQ17,subQ16,subQ15,subQ14])],"isStart":false}),makeQuery(id+"F8.opExtrude","CAP_FACE",FACE,{"disambiguationData":[OSD([subQ25,subQ24,subQ23,subQ5,subQ13,subQ22,subQ10,subQ21,subQ8,subQ20,subQ19,subQ18,subQ17,subQ16,subQ15,subQ14]),OD(0.0)],"isStart":false}),makeQuery(id+"F8.opExtrude","CAP_FACE",FACE,{"disambiguationData":[OSD([subQ25,subQ24,subQ23,subQ5,subQ13,subQ22,subQ10,subQ21,subQ8,subQ20,subQ19,subQ18,subQ17,subQ16,subQ15,subQ14]),OD(1.0)],"isStart":false})]});Q1=makeQuery(id+"F14.boolean.opBoolean","SPLIT",FACE,{"disambiguationData":[TD([subQ6])],"derivedFrom":makeQuery(id+"F12.boolean.opBoolean","MERGE",FACE,{"derivedFrom":[makeQuery(id+"F10.boolean.opBoolean","SPLIT",FACE,{"disambiguationData":[TD([makeQuery(id+"F1.opExtrude","SWEPT_FACE",FACE,{"disambiguationData":[OSD([subQ25])]})])],"derivedFrom":subQ26}),makeQuery(id+"F10.boolean.opBoolean","SPLIT",FACE,{"disambiguationData":[TD([makeQuery(id+"F1.opExtrude","SWEPT_FACE",FACE,{"disambiguationData":[OSD([subQ13])]})])],"derivedFrom":subQ26}),makeQuery(id+"F12.opExtrude","CAP_FACE",FACE,{"disambiguationData":[OSD([subQ3,subQ1,sQuery(id+"F11.wireOp",EDGE,"E64"),sQuery(id+"F11.wireOp",EDGE,"E65"),sQuery(id+"F11.wireOp",EDGE,"E70"),sQuery(id+"F11.wireOp",EDGE,"E71"),subQ0,subQ7])],"isStart":true})]})});}
            extrude(context, id + "F19", {"entities" : qUnion([Q0]), "operationType" : NewBodyOperationType.ADD, "endBound" : BoundingType.UP_TO_SURFACE, "oppositeDirection" : true, "depth" : 25 * mm, "endBoundEntityFace" : qUnion([Q1]), "offsetDistance" : 25 * mm});
        }
        {
            var Q0;
            Q0=makeQuery(id+"F10.boolean.opBoolean","MERGE",FACE,{"derivedFrom":[makeQuery(id+"F1.opExtrude","SWEPT_FACE",FACE,{"disambiguationData":[OSD([sQuery(id+"F0.wireOp",EDGE,"E9")])]}),makeQuery(id+"F10.opExtrude","SWEPT_FACE",FACE,{"disambiguationData":[OSD([sQuery(id+"F9.wireOp",EDGE,"E49")])]}),makeQuery(id+"F10.opExtrude","SWEPT_FACE",FACE,{"disambiguationData":[OSD([sQuery(id+"F9.wireOp",EDGE,"E53")])]})]});
            var sketch = newSketch(context, id + "F20", { "sketchPlane" : qUnion([Q0])});
            skLineSegment(sketch, "E83.bottom", {"start": v(66, 7) * mm, "end": v(60, 7) * mm});
            skLineSegment(sketch, "E83.top", {"start": v(66, 5) * mm, "end": v(60, 5) * mm});
            skLineSegment(sketch, "E83.left", {"start": v(66, 7) * mm, "end": v(66, 5) * mm});
            skLineSegment(sketch, "E83.right", {"start": v(60, 7) * mm, "end": v(60, 5) * mm});
            skPoint(sketch, "E83.middle", {"position": v(63, 6) * mm});
            skLineSegment(sketch, "E84", {"start": v(-2.5, 6) * mm, "end": v(63, 6) * mm, "construction": true});
            skLineSegment(sketch, "E85.bottom", {"start": v(0.5, 7) * mm, "end": v(-5.5, 7) * mm});
            skLineSegment(sketch, "E85.top", {"start": v(0.5, 5) * mm, "end": v(-5.5, 5) * mm});
            skLineSegment(sketch, "E85.left", {"start": v(0.5, 7) * mm, "end": v(0.5, 5) * mm});
            skLineSegment(sketch, "E85.right", {"start": v(-5.5, 7) * mm, "end": v(-5.5, 5) * mm});
            skPoint(sketch, "E85.middle", {"position": v(-2.5, 6) * mm});
            skLineSegment(sketch, "E86", {"start": v(63, 6) * mm, "end": v(63, 10) * mm, "construction": true});
            skSolve(sketch);
        }
        {
            var Q0;
            Q0 = qSketchRegion(id + "F20", true);
            extrude(context, id + "F21", {"entities" : qUnion([Q0]), "operationType" : NewBodyOperationType.REMOVE, "endBound" : BoundingType.THROUGH_ALL, "oppositeDirection" : true, "depth" : 25 * mm, "offsetDistance" : 25 * mm});
        }
        {
            var Q0;
            Q0=makeQuery(id+"F19.boolean.opBoolean","MERGE",FACE,{"derivedFrom":[makeQuery(id+"F12.boolean.opBoolean","MERGE",FACE,{"derivedFrom":[makeQuery(id+"F10.boolean.opBoolean","MERGE",FACE,{"derivedFrom":[makeQuery(id+"F1.opExtrude","SWEPT_FACE",FACE,{"disambiguationData":[OSD([sQuery(id+"F0.wireOp",EDGE,"E9")])]}),makeQuery(id+"F10.opExtrude","SWEPT_FACE",FACE,{"disambiguationData":[OSD([sQuery(id+"F9.wireOp",EDGE,"E49")])]}),makeQuery(id+"F10.opExtrude","SWEPT_FACE",FACE,{"disambiguationData":[OSD([sQuery(id+"F9.wireOp",EDGE,"E53")])]})]}),makeQuery(id+"F12.opExtrude","SWEPT_FACE",FACE,{"disambiguationData":[OSD([sQuery(id+"F11.wireOp",EDGE,"E70")])]})]}),makeQuery(id+"F19.opExtrude","SWEPT_FACE",FACE,{"disambiguationData":[OSD([sQuery(id+"F18.wireOp",EDGE,"E79.left")])]}),makeQuery(id+"F19.opExtrude","SWEPT_FACE",FACE,{"disambiguationData":[OSD([sQuery(id+"F18.wireOp",EDGE,"E81.left")])]})]});
            var sketch = newSketch(context, id + "F22", { "sketchPlane" : qUnion([Q0])});
            skLineSegment(sketch, "E87.bottom", {"start": v(-8, 10) * mm, "end": v(-7, 10) * mm});
            skLineSegment(sketch, "E87.top", {"start": v(-8, 0) * mm, "end": v(-7, 0) * mm});
            skLineSegment(sketch, "E87.left", {"start": v(-8, 10) * mm, "end": v(-8, 0) * mm});
            skLineSegment(sketch, "E87.right", {"start": v(-7, 10) * mm, "end": v(-7, 0) * mm});
            skSolve(sketch);
        }
        {
            var Q0;
            Q0 = qSketchRegion(id + "F22", true);
            extrude(context, id + "F23", {"entities" : qUnion([Q0]), "operationType" : NewBodyOperationType.REMOVE, "endBound" : BoundingType.THROUGH_ALL, "oppositeDirection" : true, "depth" : 25 * mm, "offsetDistance" : 25 * mm});
        }
        {
            var Q0;
            Q0=makeQuery(id+"F19.boolean.opBoolean","MERGE",FACE,{"derivedFrom":[makeQuery(id+"F12.boolean.opBoolean","MERGE",FACE,{"derivedFrom":[makeQuery(id+"F10.boolean.opBoolean","MERGE",FACE,{"derivedFrom":[makeQuery(id+"F1.opExtrude","SWEPT_FACE",FACE,{"disambiguationData":[OSD([sQuery(id+"F0.wireOp",EDGE,"E9")])]}),makeQuery(id+"F10.opExtrude","SWEPT_FACE",FACE,{"disambiguationData":[OSD([sQuery(id+"F9.wireOp",EDGE,"E49")])]}),makeQuery(id+"F10.opExtrude","SWEPT_FACE",FACE,{"disambiguationData":[OSD([sQuery(id+"F9.wireOp",EDGE,"E53")])]})]}),makeQuery(id+"F12.opExtrude","SWEPT_FACE",FACE,{"disambiguationData":[OSD([sQuery(id+"F11.wireOp",EDGE,"E70")])]})]}),makeQuery(id+"F19.opExtrude","SWEPT_FACE",FACE,{"disambiguationData":[OSD([sQuery(id+"F18.wireOp",EDGE,"E79.left")])]}),makeQuery(id+"F19.opExtrude","SWEPT_FACE",FACE,{"disambiguationData":[OSD([sQuery(id+"F18.wireOp",EDGE,"E81.left")])]})]});
            var sketch = newSketch(context, id + "F24", { "sketchPlane" : qUnion([Q0])});
            skLineSegment(sketch, "E88.0", {"start": v(0.5, 7) * mm, "end": v(-5.5, 7) * mm});
            skLineSegment(sketch, "E89.0", {"start": v(-5.5, 7) * mm, "end": v(-5.5, 5) * mm});
            skLineSegment(sketch, "E90.0", {"start": v(0.5, 5) * mm, "end": v(-5.5, 5) * mm});
            skLineSegment(sketch, "E91.0", {"start": v(0.5, 7) * mm, "end": v(0.5, 5) * mm});
            skLineSegment(sketch, "E92.0", {"start": v(66, 7) * mm, "end": v(60, 7) * mm});
            skLineSegment(sketch, "E93.0", {"start": v(66, 7) * mm, "end": v(66, 5) * mm});
            skLineSegment(sketch, "E94.0", {"start": v(66, 5) * mm, "end": v(60, 5) * mm});
            skLineSegment(sketch, "E95.0", {"start": v(60, 7) * mm, "end": v(60, 5) * mm});
            skLineSegment(sketch, "E96.0", {"start": v(70, 11) * mm, "end": v(56, 11) * mm});
            skLineSegment(sketch, "E96.1", {"start": v(70, 11) * mm, "end": v(70, 1) * mm});
            skLineSegment(sketch, "E96.2", {"start": v(70, 1) * mm, "end": v(56, 1) * mm});
            skLineSegment(sketch, "E96.3", {"start": v(56, 11) * mm, "end": v(56, 1) * mm});
            skLineSegment(sketch, "E97.0", {"start": v(4.5, 11) * mm, "end": v(-9.5, 11) * mm});
            skLineSegment(sketch, "E97.1", {"start": v(4.5, 11) * mm, "end": v(4.5, 1) * mm});
            skLineSegment(sketch, "E97.2", {"start": v(4.5, 1) * mm, "end": v(-9.5, 1) * mm});
            skLineSegment(sketch, "E97.3", {"start": v(-9.5, 11) * mm, "end": v(-9.5, 1) * mm});
            skSolve(sketch);
        }
        {
            var Q0;
            Q0 = qSketchRegion(id + "F24", true);
            var Q1;
            Q1=makeQuery(id+"F19.opExtrude","SWEPT_FACE",FACE,{"disambiguationData":[OSD([sQuery(id+"F18.wireOp",EDGE,"E81.right")])]});
            extrude(context, id + "F25", {"entities" : qUnion([Q0]), "operationType" : NewBodyOperationType.ADD, "endBound" : BoundingType.UP_TO_SURFACE, "oppositeDirection" : true, "depth" : 25 * mm, "endBoundEntityFace" : qUnion([Q1]), "offsetDistance" : 25 * mm});
        }
        {
            var Q0;
            Q0=makeQuery(id+"F19.boolean.opBoolean","MERGE",FACE,{"derivedFrom":[makeQuery(id+"F12.boolean.opBoolean","MERGE",FACE,{"derivedFrom":[makeQuery(id+"F10.boolean.opBoolean","MERGE",FACE,{"derivedFrom":[makeQuery(id+"F1.opExtrude","SWEPT_FACE",FACE,{"disambiguationData":[OSD([sQuery(id+"F0.wireOp",EDGE,"E11")])]}),makeQuery(id+"F10.opExtrude","SWEPT_FACE",FACE,{"disambiguationData":[OSD([sQuery(id+"F9.wireOp",EDGE,"E43")])]}),makeQuery(id+"F10.opExtrude","SWEPT_FACE",FACE,{"disambiguationData":[OSD([sQuery(id+"F9.wireOp",EDGE,"E58")])]})]}),makeQuery(id+"F12.opExtrude","SWEPT_FACE",FACE,{"disambiguationData":[OSD([sQuery(id+"F11.wireOp",EDGE,"E73")])]})]}),makeQuery(id+"F19.opExtrude","SWEPT_FACE",FACE,{"disambiguationData":[OSD([sQuery(id+"F18.wireOp",EDGE,"E80.left")])]}),makeQuery(id+"F19.opExtrude","SWEPT_FACE",FACE,{"disambiguationData":[OSD([sQuery(id+"F18.wireOp",EDGE,"E82.left")])]})]});
            var sketch = newSketch(context, id + "F26", { "sketchPlane" : qUnion([Q0])});
            skLineSegment(sketch, "E98.0", {"start": v(5.5, 7) * mm, "end": v(-0.5, 7) * mm});
            skLineSegment(sketch, "E99.0", {"start": v(5.5, 5) * mm, "end": v(-0.5, 5) * mm});
            skLineSegment(sketch, "E100.0", {"start": v(5.5, 5) * mm, "end": v(5.5, 7) * mm});
            skPoint(sketch, "E101.0", {"position": v(-0.5, 6) * mm});
            skLineSegment(sketch, "E102.0", {"start": v(-0.5, 5) * mm, "end": v(-0.5, 7) * mm});
            skLineSegment(sketch, "E103.0", {"start": v(9.5, 11) * mm, "end": v(-4.5, 11) * mm});
            skLineSegment(sketch, "E103.1", {"start": v(9.5, 1) * mm, "end": v(9.5, 11) * mm});
            skLineSegment(sketch, "E103.2", {"start": v(9.5, 1) * mm, "end": v(-4.5, 1) * mm});
            skLineSegment(sketch, "E103.3", {"start": v(-4.5, 1) * mm, "end": v(-4.5, 11) * mm});
            skLineSegment(sketch, "E104.0", {"start": v(-66, 5) * mm, "end": v(-60, 5) * mm});
            skLineSegment(sketch, "E105.0", {"start": v(-66, 7) * mm, "end": v(-66, 5) * mm});
            skLineSegment(sketch, "E106.0", {"start": v(-66, 7) * mm, "end": v(-60, 7) * mm});
            skLineSegment(sketch, "E107.0", {"start": v(-60, 7) * mm, "end": v(-60, 5) * mm});
            skLineSegment(sketch, "E108.0", {"start": v(-70, 1) * mm, "end": v(-56, 1) * mm});
            skLineSegment(sketch, "E108.1", {"start": v(-70, 11) * mm, "end": v(-70, 1) * mm});
            skLineSegment(sketch, "E108.2", {"start": v(-70, 11) * mm, "end": v(-56, 11) * mm});
            skLineSegment(sketch, "E108.3", {"start": v(-56, 11) * mm, "end": v(-56, 1) * mm});
            skSolve(sketch);
        }
        {
            var Q0;
            Q0 = qSketchRegion(id + "F26", true);
            var Q1;
            Q1=makeQuery(id+"F19.boolean.opBoolean","MERGE",FACE,{"derivedFrom":[makeQuery(id+"F12.boolean.opBoolean","MERGE",FACE,{"derivedFrom":[makeQuery(id+"F1.opExtrude","SWEPT_FACE",FACE,{"disambiguationData":[OSD([sQuery(id+"F0.wireOp",EDGE,"E16")])]}),makeQuery(id+"F12.opExtrude","SWEPT_FACE",FACE,{"disambiguationData":[OSD([sQuery(id+"F11.wireOp",EDGE,"E72")])]})]}),makeQuery(id+"F19.opExtrude","SWEPT_FACE",FACE,{"disambiguationData":[OSD([sQuery(id+"F18.wireOp",EDGE,"E80.right")])]})]});
            extrude(context, id + "F27", {"entities" : qUnion([Q0]), "operationType" : NewBodyOperationType.ADD, "endBound" : BoundingType.UP_TO_SURFACE, "oppositeDirection" : true, "depth" : 25 * mm, "endBoundEntityFace" : qUnion([Q1]), "offsetDistance" : 25 * mm});
        }
        {
            var Q0;
            Q0=makeQuery(id+"F27.opExtrude","SWEPT_FACE",FACE,{"disambiguationData":[OSD([sQuery(id+"F26.wireOp",EDGE,"E103.2")])]});
            var Q1;
            {var subQ0=sQuery(id+"F7.wireOp",EDGE,"E40");var subQ1=sQuery(id+"F7.wireOp",EDGE,"E39");var subQ2=sQuery(id+"F7.wireOp",EDGE,"E38");var subQ3=sQuery(id+"F7.wireOp",EDGE,"E37");var subQ4=sQuery(id+"F7.wireOp",EDGE,"E36");var subQ5=sQuery(id+"F7.wireOp",EDGE,"E35");var subQ6=sQuery(id+"F7.wireOp",EDGE,"E34");var subQ7=sQuery(id+"F7.wireOp",EDGE,"E33");var subQ8=sQuery(id+"F7.wireOp",EDGE,"E32");var subQ9=sQuery(id+"F7.wireOp",EDGE,"E31");var subQ10=sQuery(id+"F7.wireOp",EDGE,"E30");var subQ11=sQuery(id+"F7.wireOp",EDGE,"E29");var subQ12=sQuery(id+"F2.wireOp",EDGE,"E24.1");var subQ13=sQuery(id+"F2.wireOp",EDGE,"E24.0");var subQ14=sQuery(id+"F0.wireOp",EDGE,"E23");var subQ15=sQuery(id+"F0.wireOp",EDGE,"E22");var subQ16=sQuery(id+"F0.wireOp",EDGE,"E21");var subQ17=sQuery(id+"F0.wireOp",EDGE,"E20");var subQ18=sQuery(id+"F0.wireOp",EDGE,"E19");var subQ19=sQuery(id+"F0.wireOp",EDGE,"E18");var subQ20=sQuery(id+"F0.wireOp",EDGE,"E17");var subQ21=sQuery(id+"F0.wireOp",EDGE,"E16");var subQ22=sQuery(id+"F0.wireOp",EDGE,"E15");var subQ23=sQuery(id+"F0.wireOp",EDGE,"E14");var subQ24=sQuery(id+"F0.wireOp",EDGE,"E13");var subQ25=sQuery(id+"F0.wireOp",EDGE,"E12");var subQ26=sQuery(id+"F0.wireOp",EDGE,"E11");var subQ27=sQuery(id+"F0.wireOp",EDGE,"E10");var subQ28=sQuery(id+"F0.wireOp",EDGE,"E9");var subQ29=sQuery(id+"F0.wireOp",EDGE,"E8");Q1=makeQuery(id+"F12.boolean.opBoolean","MERGE",FACE,{"derivedFrom":[makeQuery(id+"F8.boolean.opBoolean","MERGE",FACE,{"derivedFrom":[makeQuery(id+"F3.boolean.opBoolean","MERGE",FACE,{"derivedFrom":[makeQuery(id+"F1.opExtrude","CAP_FACE",FACE,{"disambiguationData":[OSD([subQ29,subQ28,subQ27,subQ26,subQ25,subQ24,subQ23,subQ22,subQ21,subQ20,subQ19,subQ18,subQ17,subQ16,subQ15,subQ14])],"isStart":true}),makeQuery(id+"F3.opExtrude","CAP_FACE",FACE,{"disambiguationData":[OSD([subQ13])],"isStart":true}),makeQuery(id+"F3.opExtrude","CAP_FACE",FACE,{"disambiguationData":[OSD([subQ12])],"isStart":true})]}),makeQuery(id+"F8.opExtrude","CAP_FACE",FACE,{"disambiguationData":[OSD([subQ11,subQ10,subQ9,subQ8,subQ7,subQ6])],"isStart":true}),makeQuery(id+"F8.opExtrude","CAP_FACE",FACE,{"disambiguationData":[OSD([subQ5,subQ4,subQ3,subQ2,subQ1,subQ0])],"isStart":true})]}),makeQuery(id+"F12.opExtrude","CAP_FACE",FACE,{"disambiguationData":[OSD([subQ29,subQ28,subQ27,subQ26,subQ25,subQ24,subQ23,subQ22,subQ21,subQ20,subQ19,subQ18,subQ17,subQ16,subQ15,subQ14,subQ13,subQ12,subQ11,subQ10,subQ9,subQ8,subQ7,subQ6,subQ5,subQ4,subQ3,subQ2,subQ1,subQ0])],"isStart":false})]});}
            extrude(context, id + "F28", {"entities" : qUnion([Q0]), "operationType" : NewBodyOperationType.ADD, "endBound" : BoundingType.UP_TO_SURFACE, "depth" : 25 * mm, "endBoundEntityFace" : qUnion([Q1]), "offsetDistance" : 25 * mm});
        }
        {
            var Q0;
            Q0=makeQuery(id+"F25.opExtrude","SWEPT_FACE",FACE,{"disambiguationData":[OSD([sQuery(id+"F24.wireOp",EDGE,"E97.2")])]});
            var Q1;
            {var subQ0=sQuery(id+"F7.wireOp",EDGE,"E40");var subQ1=sQuery(id+"F7.wireOp",EDGE,"E39");var subQ2=sQuery(id+"F7.wireOp",EDGE,"E38");var subQ3=sQuery(id+"F7.wireOp",EDGE,"E37");var subQ4=sQuery(id+"F7.wireOp",EDGE,"E36");var subQ5=sQuery(id+"F7.wireOp",EDGE,"E35");var subQ6=sQuery(id+"F7.wireOp",EDGE,"E34");var subQ7=sQuery(id+"F7.wireOp",EDGE,"E33");var subQ8=sQuery(id+"F7.wireOp",EDGE,"E32");var subQ9=sQuery(id+"F7.wireOp",EDGE,"E31");var subQ10=sQuery(id+"F7.wireOp",EDGE,"E30");var subQ11=sQuery(id+"F7.wireOp",EDGE,"E29");var subQ12=sQuery(id+"F2.wireOp",EDGE,"E24.1");var subQ13=sQuery(id+"F2.wireOp",EDGE,"E24.0");var subQ14=sQuery(id+"F0.wireOp",EDGE,"E23");var subQ15=sQuery(id+"F0.wireOp",EDGE,"E22");var subQ16=sQuery(id+"F0.wireOp",EDGE,"E21");var subQ17=sQuery(id+"F0.wireOp",EDGE,"E20");var subQ18=sQuery(id+"F0.wireOp",EDGE,"E19");var subQ19=sQuery(id+"F0.wireOp",EDGE,"E18");var subQ20=sQuery(id+"F0.wireOp",EDGE,"E17");var subQ21=sQuery(id+"F0.wireOp",EDGE,"E16");var subQ22=sQuery(id+"F0.wireOp",EDGE,"E15");var subQ23=sQuery(id+"F0.wireOp",EDGE,"E14");var subQ24=sQuery(id+"F0.wireOp",EDGE,"E13");var subQ25=sQuery(id+"F0.wireOp",EDGE,"E12");var subQ26=sQuery(id+"F0.wireOp",EDGE,"E11");var subQ27=sQuery(id+"F0.wireOp",EDGE,"E10");var subQ28=sQuery(id+"F0.wireOp",EDGE,"E9");var subQ29=sQuery(id+"F0.wireOp",EDGE,"E8");Q1=makeQuery(id+"F28.boolean.opBoolean","MERGE",FACE,{"derivedFrom":[makeQuery(id+"F12.boolean.opBoolean","MERGE",FACE,{"derivedFrom":[makeQuery(id+"F8.boolean.opBoolean","MERGE",FACE,{"derivedFrom":[makeQuery(id+"F3.boolean.opBoolean","MERGE",FACE,{"derivedFrom":[makeQuery(id+"F1.opExtrude","CAP_FACE",FACE,{"disambiguationData":[OSD([subQ29,subQ28,subQ27,subQ26,subQ25,subQ24,subQ23,subQ22,subQ21,subQ20,subQ19,subQ18,subQ17,subQ16,subQ15,subQ14])],"isStart":true}),makeQuery(id+"F3.opExtrude","CAP_FACE",FACE,{"disambiguationData":[OSD([subQ13])],"isStart":true}),makeQuery(id+"F3.opExtrude","CAP_FACE",FACE,{"disambiguationData":[OSD([subQ12])],"isStart":true})]}),makeQuery(id+"F8.opExtrude","CAP_FACE",FACE,{"disambiguationData":[OSD([subQ11,subQ10,subQ9,subQ8,subQ7,subQ6])],"isStart":true}),makeQuery(id+"F8.opExtrude","CAP_FACE",FACE,{"disambiguationData":[OSD([subQ5,subQ4,subQ3,subQ2,subQ1,subQ0])],"isStart":true})]}),makeQuery(id+"F12.opExtrude","CAP_FACE",FACE,{"disambiguationData":[OSD([subQ29,subQ28,subQ27,subQ26,subQ25,subQ24,subQ23,subQ22,subQ21,subQ20,subQ19,subQ18,subQ17,subQ16,subQ15,subQ14,subQ13,subQ12,subQ11,subQ10,subQ9,subQ8,subQ7,subQ6,subQ5,subQ4,subQ3,subQ2,subQ1,subQ0])],"isStart":false})]}),makeQuery(id+"F28.opExtrude","CAP_FACE",FACE,{"disambiguationData":[OSD([subQ29,subQ28,subQ27,subQ26,subQ25,subQ24,subQ23,subQ22,subQ21,subQ20,subQ19,subQ18,subQ17,subQ16,subQ15,subQ14,subQ13,subQ12,subQ11,subQ10,subQ9,subQ8,subQ7,subQ6,subQ5,subQ4,subQ3,subQ2,subQ1,subQ0])],"isStart":false})]});}
            extrude(context, id + "F29", {"entities" : qUnion([Q0]), "operationType" : NewBodyOperationType.ADD, "endBound" : BoundingType.UP_TO_SURFACE, "depth" : 25 * mm, "endBoundEntityFace" : qUnion([Q1]), "offsetDistance" : 25 * mm});
        }
        {
            var Q0;
            {var subQ0=sQuery(id+"F7.wireOp",EDGE,"E40");var subQ1=sQuery(id+"F7.wireOp",EDGE,"E39");var subQ2=sQuery(id+"F7.wireOp",EDGE,"E38");var subQ3=sQuery(id+"F7.wireOp",EDGE,"E37");var subQ4=sQuery(id+"F7.wireOp",EDGE,"E36");var subQ5=sQuery(id+"F7.wireOp",EDGE,"E35");var subQ6=sQuery(id+"F7.wireOp",EDGE,"E34");var subQ7=sQuery(id+"F7.wireOp",EDGE,"E33");var subQ8=sQuery(id+"F7.wireOp",EDGE,"E32");var subQ9=sQuery(id+"F7.wireOp",EDGE,"E31");var subQ10=sQuery(id+"F7.wireOp",EDGE,"E30");var subQ11=sQuery(id+"F7.wireOp",EDGE,"E29");var subQ12=sQuery(id+"F2.wireOp",EDGE,"E24.1");var subQ13=sQuery(id+"F2.wireOp",EDGE,"E24.0");var subQ14=sQuery(id+"F0.wireOp",EDGE,"E23");var subQ15=sQuery(id+"F0.wireOp",EDGE,"E22");var subQ16=sQuery(id+"F0.wireOp",EDGE,"E21");var subQ17=sQuery(id+"F0.wireOp",EDGE,"E20");var subQ18=sQuery(id+"F0.wireOp",EDGE,"E19");var subQ19=sQuery(id+"F0.wireOp",EDGE,"E18");var subQ20=sQuery(id+"F0.wireOp",EDGE,"E17");var subQ21=sQuery(id+"F0.wireOp",EDGE,"E16");var subQ22=sQuery(id+"F0.wireOp",EDGE,"E15");var subQ23=sQuery(id+"F0.wireOp",EDGE,"E14");var subQ24=sQuery(id+"F0.wireOp",EDGE,"E13");var subQ25=sQuery(id+"F0.wireOp",EDGE,"E12");var subQ26=sQuery(id+"F0.wireOp",EDGE,"E11");var subQ27=sQuery(id+"F0.wireOp",EDGE,"E10");var subQ28=sQuery(id+"F0.wireOp",EDGE,"E9");var subQ29=sQuery(id+"F0.wireOp",EDGE,"E8");Q0=makeQuery(id+"F29.boolean.opBoolean","MERGE",FACE,{"derivedFrom":[makeQuery(id+"F28.boolean.opBoolean","MERGE",FACE,{"derivedFrom":[makeQuery(id+"F12.boolean.opBoolean","MERGE",FACE,{"derivedFrom":[makeQuery(id+"F8.boolean.opBoolean","MERGE",FACE,{"derivedFrom":[makeQuery(id+"F3.boolean.opBoolean","MERGE",FACE,{"derivedFrom":[makeQuery(id+"F1.opExtrude","CAP_FACE",FACE,{"disambiguationData":[OSD([subQ29,subQ28,subQ27,subQ26,subQ25,subQ24,subQ23,subQ22,subQ21,subQ20,subQ19,subQ18,subQ17,subQ16,subQ15,subQ14])],"isStart":true}),makeQuery(id+"F3.opExtrude","CAP_FACE",FACE,{"disambiguationData":[OSD([subQ13])],"isStart":true}),makeQuery(id+"F3.opExtrude","CAP_FACE",FACE,{"disambiguationData":[OSD([subQ12])],"isStart":true})]}),makeQuery(id+"F8.opExtrude","CAP_FACE",FACE,{"disambiguationData":[OSD([subQ11,subQ10,subQ9,subQ8,subQ7,subQ6])],"isStart":true}),makeQuery(id+"F8.opExtrude","CAP_FACE",FACE,{"disambiguationData":[OSD([subQ5,subQ4,subQ3,subQ2,subQ1,subQ0])],"isStart":true})]}),makeQuery(id+"F12.opExtrude","CAP_FACE",FACE,{"disambiguationData":[OSD([subQ29,subQ28,subQ27,subQ26,subQ25,subQ24,subQ23,subQ22,subQ21,subQ20,subQ19,subQ18,subQ17,subQ16,subQ15,subQ14,subQ13,subQ12,subQ11,subQ10,subQ9,subQ8,subQ7,subQ6,subQ5,subQ4,subQ3,subQ2,subQ1,subQ0])],"isStart":false})]}),makeQuery(id+"F28.opExtrude","CAP_FACE",FACE,{"disambiguationData":[OSD([subQ29,subQ28,subQ27,subQ26,subQ25,subQ24,subQ23,subQ22,subQ21,subQ20,subQ19,subQ18,subQ17,subQ16,subQ15,subQ14,subQ13,subQ12,subQ11,subQ10,subQ9,subQ8,subQ7,subQ6,subQ5,subQ4,subQ3,subQ2,subQ1,subQ0])],"isStart":false})]}),makeQuery(id+"F29.opExtrude","CAP_FACE",FACE,{"disambiguationData":[OSD([subQ29,subQ28,subQ27,subQ26,subQ25,subQ24,subQ23,subQ22,subQ21,subQ20,subQ19,subQ18,subQ17,subQ16,subQ15,subQ14,subQ13,subQ12,subQ11,subQ10,subQ9,subQ8,subQ7,subQ6,subQ5,subQ4,subQ3,subQ2,subQ1,subQ0])],"isStart":false})]});}
            var sketch = newSketch(context, id + "F30", { "sketchPlane" : qUnion([Q0])});
            skLineSegment(sketch, "E109", {"start": v(-4, -72) * mm, "end": v(9.5, -72) * mm});
            skLineSegment(sketch, "E110", {"start": v(9.5, -72) * mm, "end": v(9.5, -94) * mm});
            skLineSegment(sketch, "E111", {"start": v(9.5, -94) * mm, "end": v(39.5, -94) * mm});
            skLineSegment(sketch, "E112", {"start": v(39.5, -94) * mm, "end": v(39.5, -72) * mm});
            skLineSegment(sketch, "E113", {"start": v(39.5, -72) * mm, "end": v(53, -72) * mm});
            skLineSegment(sketch, "E114", {"start": v(53, -72) * mm, "end": v(53, -66) * mm});
            skLineSegment(sketch, "E115", {"start": v(53, -66) * mm, "end": v(-4, -66) * mm});
            skLineSegment(sketch, "E116", {"start": v(-4, -66) * mm, "end": v(-4, -72) * mm});
            skLineSegment(sketch, "E117", {"start": v(24.5, -100) * mm, "end": v(24.5, -94) * mm, "construction": true});
            skSolve(sketch);
        }
        {
            var Q0;
            Q0 = qSketchRegion(id + "F30", true);
            var Q1;
            {var subQ2=sQuery(id+"F11.wireOp",EDGE,"E71");var subQ4=sQuery(id+"F0.wireOp",EDGE,"E9");var subQ5=makeQuery(id+"F1.opExtrude","SWEPT_FACE",FACE,{"disambiguationData":[OSD([subQ4])]});var subQ6=sQuery(id+"F11.wireOp",EDGE,"E70");var subQ8=sQuery(id+"F11.wireOp",EDGE,"E60");var subQ9=makeQuery(id+"F12.opExtrude","SWEPT_FACE",FACE,{"disambiguationData":[OSD([subQ8])]});var subQ11=sQuery(id+"F0.wireOp",EDGE,"E20");var subQ15=sQuery(id+"F11.wireOp",EDGE,"E62");var subQ19=sQuery(id+"F0.wireOp",EDGE,"E22");var subQ21=sQuery(id+"F0.wireOp",EDGE,"E14");var subQ22=sQuery(id+"F0.wireOp",EDGE,"E12");var subQ23=sQuery(id+"F0.wireOp",EDGE,"E16");var subQ24=sQuery(id+"F0.wireOp",EDGE,"E11");var subQ25=sQuery(id+"F0.wireOp",EDGE,"E23");var subQ26=sQuery(id+"F0.wireOp",EDGE,"E21");var subQ27=sQuery(id+"F0.wireOp",EDGE,"E19");var subQ28=sQuery(id+"F0.wireOp",EDGE,"E18");var subQ29=sQuery(id+"F0.wireOp",EDGE,"E17");var subQ30=sQuery(id+"F0.wireOp",EDGE,"E15");var subQ31=sQuery(id+"F0.wireOp",EDGE,"E13");var subQ32=sQuery(id+"F0.wireOp",EDGE,"E10");var subQ33=sQuery(id+"F0.wireOp",EDGE,"E8");var subQ34=makeQuery(id+"F8.boolean.opBoolean","MERGE",FACE,{"derivedFrom":[makeQuery(id+"F1.opExtrude","CAP_FACE",FACE,{"disambiguationData":[OSD([subQ33,subQ4,subQ32,subQ24,subQ22,subQ31,subQ21,subQ30,subQ23,subQ29,subQ28,subQ27,subQ11,subQ26,subQ19,subQ25])],"isStart":false}),makeQuery(id+"F8.opExtrude","CAP_FACE",FACE,{"disambiguationData":[OSD([subQ33,subQ4,subQ32,subQ24,subQ22,subQ31,subQ21,subQ30,subQ23,subQ29,subQ28,subQ27,subQ11,subQ26,subQ19,subQ25]),OD(0.0)],"isStart":false}),makeQuery(id+"F8.opExtrude","CAP_FACE",FACE,{"disambiguationData":[OSD([subQ33,subQ4,subQ32,subQ24,subQ22,subQ31,subQ21,subQ30,subQ23,subQ29,subQ28,subQ27,subQ11,subQ26,subQ19,subQ25]),OD(1.0)],"isStart":false})]});Q1=makeQuery(id+"F25.boolean.opBoolean","SPLIT",FACE,{"disambiguationData":[TD([subQ9])],"derivedFrom":makeQuery(id+"F21.boolean.opBoolean","MERGE",FACE,{"derivedFrom":[makeQuery(id+"F14.boolean.opBoolean","SPLIT",FACE,{"disambiguationData":[TD([subQ5])],"derivedFrom":makeQuery(id+"F12.boolean.opBoolean","MERGE",FACE,{"derivedFrom":[makeQuery(id+"F10.boolean.opBoolean","SPLIT",FACE,{"disambiguationData":[TD([makeQuery(id+"F1.opExtrude","SWEPT_FACE",FACE,{"disambiguationData":[OSD([subQ33])]})])],"derivedFrom":subQ34}),makeQuery(id+"F10.boolean.opBoolean","SPLIT",FACE,{"disambiguationData":[TD([makeQuery(id+"F1.opExtrude","SWEPT_FACE",FACE,{"disambiguationData":[OSD([subQ22])]})])],"derivedFrom":subQ34}),makeQuery(id+"F12.opExtrude","CAP_FACE",FACE,{"disambiguationData":[OSD([subQ8,subQ15,sQuery(id+"F11.wireOp",EDGE,"E64"),sQuery(id+"F11.wireOp",EDGE,"E65"),subQ6,subQ2,sQuery(id+"F11.wireOp",EDGE,"E72"),sQuery(id+"F11.wireOp",EDGE,"E73")])],"isStart":true})]})}),makeQuery(id+"F21.opExtrude","SWEPT_FACE",FACE,{"disambiguationData":[OSD([sQuery(id+"F20.wireOp",EDGE,"E83.top")])]})]})});}
            extrude(context, id + "F31", {"entities" : qUnion([Q0]), "operationType" : NewBodyOperationType.ADD, "endBound" : BoundingType.UP_TO_SURFACE, "oppositeDirection" : true, "depth" : 25 * mm, "endBoundEntityFace" : qUnion([Q1]), "offsetDistance" : 25 * mm});
        }
        {
            var Q0;
            {var subQ3=sQuery(id+"F11.wireOp",EDGE,"E72");var subQ5=sQuery(id+"F11.wireOp",EDGE,"E60");var subQ6=makeQuery(id+"F12.opExtrude","SWEPT_FACE",FACE,{"disambiguationData":[OSD([subQ5])]});var subQ15=sQuery(id+"F0.wireOp",EDGE,"E11");var subQ16=makeQuery(id+"F1.opExtrude","SWEPT_FACE",FACE,{"disambiguationData":[OSD([subQ15])]});var subQ17=sQuery(id+"F11.wireOp",EDGE,"E73");var subQ19=sQuery(id+"F0.wireOp",EDGE,"E16");var subQ21=sQuery(id+"F11.wireOp",EDGE,"E62");var subQ25=makeQuery(id+"F21.opExtrude","SWEPT_FACE",FACE,{"disambiguationData":[OSD([sQuery(id+"F20.wireOp",EDGE,"E83.top")])]});var subQ27=sQuery(id+"F0.wireOp",EDGE,"E14");var subQ29=sQuery(id+"F11.wireOp",EDGE,"E71");var subQ30=sQuery(id+"F11.wireOp",EDGE,"E70");var subQ31=sQuery(id+"F0.wireOp",EDGE,"E12");var subQ32=sQuery(id+"F0.wireOp",EDGE,"E23");var subQ33=sQuery(id+"F0.wireOp",EDGE,"E22");var subQ34=sQuery(id+"F0.wireOp",EDGE,"E21");var subQ35=sQuery(id+"F0.wireOp",EDGE,"E20");var subQ36=sQuery(id+"F0.wireOp",EDGE,"E19");var subQ37=sQuery(id+"F0.wireOp",EDGE,"E18");var subQ38=sQuery(id+"F0.wireOp",EDGE,"E17");var subQ39=sQuery(id+"F0.wireOp",EDGE,"E15");var subQ40=sQuery(id+"F0.wireOp",EDGE,"E13");var subQ41=sQuery(id+"F0.wireOp",EDGE,"E10");var subQ42=sQuery(id+"F0.wireOp",EDGE,"E9");var subQ43=sQuery(id+"F0.wireOp",EDGE,"E8");var subQ44=makeQuery(id+"F8.boolean.opBoolean","MERGE",FACE,{"derivedFrom":[makeQuery(id+"F1.opExtrude","CAP_FACE",FACE,{"disambiguationData":[OSD([subQ43,subQ42,subQ41,subQ15,subQ31,subQ40,subQ27,subQ39,subQ19,subQ38,subQ37,subQ36,subQ35,subQ34,subQ33,subQ32])],"isStart":false}),makeQuery(id+"F8.opExtrude","CAP_FACE",FACE,{"disambiguationData":[OSD([subQ43,subQ42,subQ41,subQ15,subQ31,subQ40,subQ27,subQ39,subQ19,subQ38,subQ37,subQ36,subQ35,subQ34,subQ33,subQ32]),OD(0.0)],"isStart":false}),makeQuery(id+"F8.opExtrude","CAP_FACE",FACE,{"disambiguationData":[OSD([subQ43,subQ42,subQ41,subQ15,subQ31,subQ40,subQ27,subQ39,subQ19,subQ38,subQ37,subQ36,subQ35,subQ34,subQ33,subQ32]),OD(1.0)],"isStart":false})]});var subQ47=makeQuery(id+"F1.opExtrude","SWEPT_FACE",FACE,{"disambiguationData":[OSD([subQ42])]});var subQ51=makeQuery(id+"F12.boolean.opBoolean","MERGE",FACE,{"derivedFrom":[makeQuery(id+"F10.boolean.opBoolean","SPLIT",FACE,{"disambiguationData":[TD([makeQuery(id+"F1.opExtrude","SWEPT_FACE",FACE,{"disambiguationData":[OSD([subQ43])]})])],"derivedFrom":subQ44}),makeQuery(id+"F10.boolean.opBoolean","SPLIT",FACE,{"disambiguationData":[TD([makeQuery(id+"F1.opExtrude","SWEPT_FACE",FACE,{"disambiguationData":[OSD([subQ31])]})])],"derivedFrom":subQ44}),makeQuery(id+"F12.opExtrude","CAP_FACE",FACE,{"disambiguationData":[OSD([subQ5,subQ21,sQuery(id+"F11.wireOp",EDGE,"E64"),sQuery(id+"F11.wireOp",EDGE,"E65"),subQ30,subQ29,subQ3,subQ17])],"isStart":true})]});Q0=makeQuery(id+"F31.boolean.opBoolean","MERGE",FACE,{"derivedFrom":[makeQuery(id+"F25.boolean.opBoolean","SPLIT",FACE,{"disambiguationData":[TD([subQ6])],"derivedFrom":makeQuery(id+"F21.boolean.opBoolean","MERGE",FACE,{"derivedFrom":[makeQuery(id+"F14.boolean.opBoolean","SPLIT",FACE,{"disambiguationData":[TD([subQ47])],"derivedFrom":subQ51}),subQ25]})}),makeQuery(id+"F27.boolean.opBoolean","SPLIT",FACE,{"disambiguationData":[TD([subQ6])],"derivedFrom":makeQuery(id+"F21.boolean.opBoolean","MERGE",FACE,{"derivedFrom":[makeQuery(id+"F14.boolean.opBoolean","SPLIT",FACE,{"disambiguationData":[TD([subQ16])],"derivedFrom":subQ51}),subQ25]})}),makeQuery(id+"F31.opExtrude","CAP_FACE",FACE,{"disambiguationData":[OSD([sQuery(id+"F30.wireOp",EDGE,"E109"),sQuery(id+"F30.wireOp",EDGE,"E110"),sQuery(id+"F30.wireOp",EDGE,"E111"),sQuery(id+"F30.wireOp",EDGE,"E112"),sQuery(id+"F30.wireOp",EDGE,"E113"),sQuery(id+"F30.wireOp",EDGE,"E114"),sQuery(id+"F30.wireOp",EDGE,"E115"),sQuery(id+"F30.wireOp",EDGE,"E116")])],"isStart":false})]});}
            var sketch = newSketch(context, id + "F32", { "sketchPlane" : qUnion([Q0])});
            skLineSegment(sketch, "E118.0", {"start": v(39.5, 100) * mm, "end": v(39.5, 94) * mm});
            skLineSegment(sketch, "E118.1", {"start": v(9.5, 100) * mm, "end": v(9.5, 94) * mm});
            skLineSegment(sketch, "E119.0", {"start": v(53, 94) * mm, "end": v(53, 72) * mm});
            skLineSegment(sketch, "E119.1", {"start": v(53, 94) * mm, "end": v(39.5, 94) * mm});
            skLineSegment(sketch, "E119.2", {"start": v(9.5, 94) * mm, "end": v(-4, 94) * mm});
            skLineSegment(sketch, "E119.3", {"start": v(-4, 94) * mm, "end": v(-4, 72) * mm});
            skLineSegment(sketch, "E120.0", {"start": v(-10, 100) * mm, "end": v(9.5, 100) * mm});
            skLineSegment(sketch, "E120.1", {"start": v(39.5, 100) * mm, "end": v(59, 100) * mm});
            skLineSegment(sketch, "E121", {"start": v(-4, 72) * mm, "end": v(-10, 72) * mm});
            skLineSegment(sketch, "E122", {"start": v(-10, 72) * mm, "end": v(-10, 100) * mm});
            skLineSegment(sketch, "E123", {"start": v(53, 72) * mm, "end": v(59, 72) * mm});
            skLineSegment(sketch, "E124", {"start": v(59, 72) * mm, "end": v(59, 100) * mm});
            skSolve(sketch);
        }
        {
            var Q0;
            Q0 = qSketchRegion(id + "F32", true);
            extrude(context, id + "F33", {"entities" : qUnion([Q0]), "operationType" : NewBodyOperationType.REMOVE, "oppositeDirection" : true, "depth" : 25 * mm, "offsetDistance" : 25 * mm});
        }
        {
            var Q0;
            {var subQ3=sQuery(id+"F11.wireOp",EDGE,"E72");var subQ5=sQuery(id+"F11.wireOp",EDGE,"E60");var subQ6=makeQuery(id+"F12.opExtrude","SWEPT_FACE",FACE,{"disambiguationData":[OSD([subQ5])]});var subQ15=sQuery(id+"F0.wireOp",EDGE,"E11");var subQ16=makeQuery(id+"F1.opExtrude","SWEPT_FACE",FACE,{"disambiguationData":[OSD([subQ15])]});var subQ17=sQuery(id+"F11.wireOp",EDGE,"E73");var subQ19=sQuery(id+"F0.wireOp",EDGE,"E16");var subQ21=sQuery(id+"F11.wireOp",EDGE,"E62");var subQ25=makeQuery(id+"F21.opExtrude","SWEPT_FACE",FACE,{"disambiguationData":[OSD([sQuery(id+"F20.wireOp",EDGE,"E83.top")])]});var subQ27=sQuery(id+"F0.wireOp",EDGE,"E14");var subQ29=sQuery(id+"F11.wireOp",EDGE,"E71");var subQ30=sQuery(id+"F11.wireOp",EDGE,"E70");var subQ31=sQuery(id+"F0.wireOp",EDGE,"E12");var subQ32=sQuery(id+"F0.wireOp",EDGE,"E23");var subQ33=sQuery(id+"F0.wireOp",EDGE,"E22");var subQ34=sQuery(id+"F0.wireOp",EDGE,"E21");var subQ35=sQuery(id+"F0.wireOp",EDGE,"E20");var subQ36=sQuery(id+"F0.wireOp",EDGE,"E19");var subQ37=sQuery(id+"F0.wireOp",EDGE,"E18");var subQ38=sQuery(id+"F0.wireOp",EDGE,"E17");var subQ39=sQuery(id+"F0.wireOp",EDGE,"E15");var subQ40=sQuery(id+"F0.wireOp",EDGE,"E13");var subQ41=sQuery(id+"F0.wireOp",EDGE,"E10");var subQ42=sQuery(id+"F0.wireOp",EDGE,"E9");var subQ43=sQuery(id+"F0.wireOp",EDGE,"E8");var subQ44=makeQuery(id+"F8.boolean.opBoolean","MERGE",FACE,{"derivedFrom":[makeQuery(id+"F1.opExtrude","CAP_FACE",FACE,{"disambiguationData":[OSD([subQ43,subQ42,subQ41,subQ15,subQ31,subQ40,subQ27,subQ39,subQ19,subQ38,subQ37,subQ36,subQ35,subQ34,subQ33,subQ32])],"isStart":false}),makeQuery(id+"F8.opExtrude","CAP_FACE",FACE,{"disambiguationData":[OSD([subQ43,subQ42,subQ41,subQ15,subQ31,subQ40,subQ27,subQ39,subQ19,subQ38,subQ37,subQ36,subQ35,subQ34,subQ33,subQ32]),OD(0.0)],"isStart":false}),makeQuery(id+"F8.opExtrude","CAP_FACE",FACE,{"disambiguationData":[OSD([subQ43,subQ42,subQ41,subQ15,subQ31,subQ40,subQ27,subQ39,subQ19,subQ38,subQ37,subQ36,subQ35,subQ34,subQ33,subQ32]),OD(1.0)],"isStart":false})]});var subQ47=makeQuery(id+"F1.opExtrude","SWEPT_FACE",FACE,{"disambiguationData":[OSD([subQ42])]});var subQ51=makeQuery(id+"F12.boolean.opBoolean","MERGE",FACE,{"derivedFrom":[makeQuery(id+"F10.boolean.opBoolean","SPLIT",FACE,{"disambiguationData":[TD([makeQuery(id+"F1.opExtrude","SWEPT_FACE",FACE,{"disambiguationData":[OSD([subQ43])]})])],"derivedFrom":subQ44}),makeQuery(id+"F10.boolean.opBoolean","SPLIT",FACE,{"disambiguationData":[TD([makeQuery(id+"F1.opExtrude","SWEPT_FACE",FACE,{"disambiguationData":[OSD([subQ31])]})])],"derivedFrom":subQ44}),makeQuery(id+"F12.opExtrude","CAP_FACE",FACE,{"disambiguationData":[OSD([subQ5,subQ21,sQuery(id+"F11.wireOp",EDGE,"E64"),sQuery(id+"F11.wireOp",EDGE,"E65"),subQ30,subQ29,subQ3,subQ17])],"isStart":true})]});Q0=makeQuery(id+"F31.boolean.opBoolean","MERGE",FACE,{"derivedFrom":[makeQuery(id+"F25.boolean.opBoolean","SPLIT",FACE,{"disambiguationData":[TD([subQ6])],"derivedFrom":makeQuery(id+"F21.boolean.opBoolean","MERGE",FACE,{"derivedFrom":[makeQuery(id+"F14.boolean.opBoolean","SPLIT",FACE,{"disambiguationData":[TD([subQ47])],"derivedFrom":subQ51}),subQ25]})}),makeQuery(id+"F27.boolean.opBoolean","SPLIT",FACE,{"disambiguationData":[TD([subQ6])],"derivedFrom":makeQuery(id+"F21.boolean.opBoolean","MERGE",FACE,{"derivedFrom":[makeQuery(id+"F14.boolean.opBoolean","SPLIT",FACE,{"disambiguationData":[TD([subQ16])],"derivedFrom":subQ51}),subQ25]})}),makeQuery(id+"F31.opExtrude","CAP_FACE",FACE,{"disambiguationData":[OSD([sQuery(id+"F30.wireOp",EDGE,"E109"),sQuery(id+"F30.wireOp",EDGE,"E110"),sQuery(id+"F30.wireOp",EDGE,"E111"),sQuery(id+"F30.wireOp",EDGE,"E112"),sQuery(id+"F30.wireOp",EDGE,"E113"),sQuery(id+"F30.wireOp",EDGE,"E114"),sQuery(id+"F30.wireOp",EDGE,"E115"),sQuery(id+"F30.wireOp",EDGE,"E116")])],"isStart":false})]});}
            var sketch = newSketch(context, id + "F34", { "sketchPlane" : qUnion([Q0])});
            skLineSegment(sketch, "E125", {"start": v(35.5, 82) * mm, "end": v(35.5, 94) * mm});
            skLineSegment(sketch, "E126", {"start": v(35.5, 94) * mm, "end": v(13.5, 94) * mm});
            skLineSegment(sketch, "E127", {"start": v(13.5, 94) * mm, "end": v(13.5, 82) * mm});
            skArc(sketch, "E128", {"start": v(13.5, 82) * mm, "mid": v(24.5, 71) * mm, "end": v(35.5, 82) * mm});
            skSolve(sketch);
        }
        {
            var Q0;
            Q0 = qSketchRegion(id + "F34", true);
            extrude(context, id + "F35", {"entities" : qUnion([Q0]), "operationType" : NewBodyOperationType.REMOVE, "oppositeDirection" : true, "depth" : 25 * mm, "offsetDistance" : 25 * mm});
        }
        {
            var Q0;
            {var subQ3=sQuery(id+"F11.wireOp",EDGE,"E72");var subQ5=sQuery(id+"F11.wireOp",EDGE,"E60");var subQ6=makeQuery(id+"F12.opExtrude","SWEPT_FACE",FACE,{"disambiguationData":[OSD([subQ5])]});var subQ15=sQuery(id+"F0.wireOp",EDGE,"E11");var subQ16=makeQuery(id+"F1.opExtrude","SWEPT_FACE",FACE,{"disambiguationData":[OSD([subQ15])]});var subQ17=sQuery(id+"F11.wireOp",EDGE,"E73");var subQ19=sQuery(id+"F0.wireOp",EDGE,"E16");var subQ21=sQuery(id+"F11.wireOp",EDGE,"E62");var subQ25=makeQuery(id+"F21.opExtrude","SWEPT_FACE",FACE,{"disambiguationData":[OSD([sQuery(id+"F20.wireOp",EDGE,"E83.top")])]});var subQ27=sQuery(id+"F0.wireOp",EDGE,"E14");var subQ29=sQuery(id+"F11.wireOp",EDGE,"E71");var subQ30=sQuery(id+"F11.wireOp",EDGE,"E70");var subQ31=sQuery(id+"F0.wireOp",EDGE,"E12");var subQ32=sQuery(id+"F0.wireOp",EDGE,"E23");var subQ33=sQuery(id+"F0.wireOp",EDGE,"E22");var subQ34=sQuery(id+"F0.wireOp",EDGE,"E21");var subQ35=sQuery(id+"F0.wireOp",EDGE,"E20");var subQ36=sQuery(id+"F0.wireOp",EDGE,"E19");var subQ37=sQuery(id+"F0.wireOp",EDGE,"E18");var subQ38=sQuery(id+"F0.wireOp",EDGE,"E17");var subQ39=sQuery(id+"F0.wireOp",EDGE,"E15");var subQ40=sQuery(id+"F0.wireOp",EDGE,"E13");var subQ41=sQuery(id+"F0.wireOp",EDGE,"E10");var subQ42=sQuery(id+"F0.wireOp",EDGE,"E9");var subQ43=sQuery(id+"F0.wireOp",EDGE,"E8");var subQ44=makeQuery(id+"F8.boolean.opBoolean","MERGE",FACE,{"derivedFrom":[makeQuery(id+"F1.opExtrude","CAP_FACE",FACE,{"disambiguationData":[OSD([subQ43,subQ42,subQ41,subQ15,subQ31,subQ40,subQ27,subQ39,subQ19,subQ38,subQ37,subQ36,subQ35,subQ34,subQ33,subQ32])],"isStart":false}),makeQuery(id+"F8.opExtrude","CAP_FACE",FACE,{"disambiguationData":[OSD([subQ43,subQ42,subQ41,subQ15,subQ31,subQ40,subQ27,subQ39,subQ19,subQ38,subQ37,subQ36,subQ35,subQ34,subQ33,subQ32]),OD(0.0)],"isStart":false}),makeQuery(id+"F8.opExtrude","CAP_FACE",FACE,{"disambiguationData":[OSD([subQ43,subQ42,subQ41,subQ15,subQ31,subQ40,subQ27,subQ39,subQ19,subQ38,subQ37,subQ36,subQ35,subQ34,subQ33,subQ32]),OD(1.0)],"isStart":false})]});var subQ47=makeQuery(id+"F1.opExtrude","SWEPT_FACE",FACE,{"disambiguationData":[OSD([subQ42])]});var subQ51=makeQuery(id+"F12.boolean.opBoolean","MERGE",FACE,{"derivedFrom":[makeQuery(id+"F10.boolean.opBoolean","SPLIT",FACE,{"disambiguationData":[TD([makeQuery(id+"F1.opExtrude","SWEPT_FACE",FACE,{"disambiguationData":[OSD([subQ43])]})])],"derivedFrom":subQ44}),makeQuery(id+"F10.boolean.opBoolean","SPLIT",FACE,{"disambiguationData":[TD([makeQuery(id+"F1.opExtrude","SWEPT_FACE",FACE,{"disambiguationData":[OSD([subQ31])]})])],"derivedFrom":subQ44}),makeQuery(id+"F12.opExtrude","CAP_FACE",FACE,{"disambiguationData":[OSD([subQ5,subQ21,sQuery(id+"F11.wireOp",EDGE,"E64"),sQuery(id+"F11.wireOp",EDGE,"E65"),subQ30,subQ29,subQ3,subQ17])],"isStart":true})]});Q0=makeQuery(id+"F31.boolean.opBoolean","MERGE",FACE,{"derivedFrom":[makeQuery(id+"F25.boolean.opBoolean","SPLIT",FACE,{"disambiguationData":[TD([subQ6])],"derivedFrom":makeQuery(id+"F21.boolean.opBoolean","MERGE",FACE,{"derivedFrom":[makeQuery(id+"F14.boolean.opBoolean","SPLIT",FACE,{"disambiguationData":[TD([subQ47])],"derivedFrom":subQ51}),subQ25]})}),makeQuery(id+"F27.boolean.opBoolean","SPLIT",FACE,{"disambiguationData":[TD([subQ6])],"derivedFrom":makeQuery(id+"F21.boolean.opBoolean","MERGE",FACE,{"derivedFrom":[makeQuery(id+"F14.boolean.opBoolean","SPLIT",FACE,{"disambiguationData":[TD([subQ16])],"derivedFrom":subQ51}),subQ25]})}),makeQuery(id+"F31.opExtrude","CAP_FACE",FACE,{"disambiguationData":[OSD([sQuery(id+"F30.wireOp",EDGE,"E109"),sQuery(id+"F30.wireOp",EDGE,"E110"),sQuery(id+"F30.wireOp",EDGE,"E111"),sQuery(id+"F30.wireOp",EDGE,"E112"),sQuery(id+"F30.wireOp",EDGE,"E113"),sQuery(id+"F30.wireOp",EDGE,"E114"),sQuery(id+"F30.wireOp",EDGE,"E115"),sQuery(id+"F30.wireOp",EDGE,"E116")])],"isStart":false})]});}
            var sketch = newSketch(context, id + "F36", { "sketchPlane" : qUnion([Q0])});
            skLineSegment(sketch, "E129.bottom", {"start": v(59, 72) * mm, "end": v(39.5, 72) * mm});
            skLineSegment(sketch, "E129.top", {"start": v(59, 70) * mm, "end": v(39.5, 70) * mm});
            skLineSegment(sketch, "E129.left", {"start": v(59, 72) * mm, "end": v(59, 70) * mm});
            skLineSegment(sketch, "E129.right", {"start": v(39.5, 72) * mm, "end": v(39.5, 70) * mm});
            skLineSegment(sketch, "E130.bottom", {"start": v(-10, 72) * mm, "end": v(9.5, 72) * mm});
            skLineSegment(sketch, "E130.top", {"start": v(-10, 70) * mm, "end": v(9.5, 70) * mm});
            skLineSegment(sketch, "E130.left", {"start": v(-10, 72) * mm, "end": v(-10, 70) * mm});
            skLineSegment(sketch, "E130.right", {"start": v(9.5, 72) * mm, "end": v(9.5, 70) * mm});
            skSolve(sketch);
        }
        {
            var Q0;
            Q0 = qSketchRegion(id + "F36", true);
            extrude(context, id + "F37", {"entities" : qUnion([Q0]), "operationType" : NewBodyOperationType.REMOVE, "oppositeDirection" : true, "depth" : 25 * mm, "offsetDistance" : 25 * mm});
        }
        {
            var Q0;
            Q0=makeQuery(id+"F19.boolean.opBoolean","MERGE",FACE,{"derivedFrom":[makeQuery(id+"F10.boolean.opBoolean","MERGE",FACE,{"derivedFrom":[makeQuery(id+"F3.opExtrude","CAP_FACE",FACE,{"disambiguationData":[OSD([sQuery(id+"F2.wireOp",EDGE,"E24.3")])],"isStart":false}),makeQuery(id+"F10.opExtrude","CAP_FACE",FACE,{"disambiguationData":[OSD([sQuery(id+"F2.wireOp",EDGE,"E24.0")]),OD(3.0)],"isStart":false})]}),makeQuery(id+"F19.opExtrude","CAP_FACE",FACE,{"disambiguationData":[OSD([sQuery(id+"F18.wireOp",EDGE,"E80.bottom"),sQuery(id+"F18.wireOp",EDGE,"E80.top"),sQuery(id+"F18.wireOp",EDGE,"E80.left"),sQuery(id+"F18.wireOp",EDGE,"E80.right")])],"isStart":true})]});
            var sketch = newSketch(context, id + "F38", { "sketchPlane" : qUnion([Q0])});
            skLineSegment(sketch, "E131.bottom", {"start": v(-4, 56) * mm, "end": v(-10, 56) * mm});
            skLineSegment(sketch, "E131.top", {"start": v(-4, 55) * mm, "end": v(-10, 55) * mm});
            skLineSegment(sketch, "E131.left", {"start": v(-4, 56) * mm, "end": v(-4, 55) * mm});
            skLineSegment(sketch, "E131.right", {"start": v(-10, 56) * mm, "end": v(-10, 55) * mm});
            skLineSegment(sketch, "E132.bottom", {"start": v(53, 56) * mm, "end": v(59, 56) * mm});
            skLineSegment(sketch, "E132.top", {"start": v(53, 55) * mm, "end": v(59, 55) * mm});
            skLineSegment(sketch, "E132.left", {"start": v(53, 56) * mm, "end": v(53, 55) * mm});
            skLineSegment(sketch, "E132.right", {"start": v(59, 56) * mm, "end": v(59, 55) * mm});
            skSolve(sketch);
        }
        {
            var Q0;
            Q0 = qSketchRegion(id + "F38", true);
            var Q1;
            Q1=makeQuery(id+"F25.opExtrude","SWEPT_FACE",FACE,{"disambiguationData":[OSD([sQuery(id+"F24.wireOp",EDGE,"E96.0")])]});
            extrude(context, id + "F39", {"entities" : qUnion([Q0]), "operationType" : NewBodyOperationType.ADD, "endBound" : BoundingType.UP_TO_SURFACE, "depth" : 25 * mm, "endBoundEntityFace" : qUnion([Q1]), "offsetDistance" : 25 * mm});
        }
        {
            var Q0;
            Q0=makeQuery(id+"F39.opExtrude","TWEAK_EDGE",EDGE,{"derivedFrom":[makeQuery(id+"F25.opExtrude","SWEPT_FACE",FACE,{"disambiguationData":[OSD([sQuery(id+"F24.wireOp",EDGE,"E96.0")])]}),makeQuery(id+"F38.imprint","IMPRINT",EDGE,{"derivedFrom":sQuery(id+"F38.wireOp",EDGE,"E131.top")})]});
            var Q1;
            Q1=makeQuery(id+"F27.opExtrude","SWEPT_EDGE",EDGE,{"disambiguationData":[OSD([sQuery(id+"F26.wireOp",EDGE,"E108.1"),sQuery(id+"F26.wireOp",EDGE,"E108.2")])]});
            var Q2;
            Q2=makeQuery(id+"F39.opExtrude","TWEAK_EDGE",EDGE,{"derivedFrom":[makeQuery(id+"F25.opExtrude","SWEPT_FACE",FACE,{"disambiguationData":[OSD([sQuery(id+"F24.wireOp",EDGE,"E96.0")])]}),makeQuery(id+"F38.imprint","IMPRINT",EDGE,{"derivedFrom":sQuery(id+"F38.wireOp",EDGE,"E132.top")})]});
            var Q3;
            Q3=makeQuery(id+"F25.opExtrude","SWEPT_EDGE",EDGE,{"disambiguationData":[OSD([sQuery(id+"F24.wireOp",EDGE,"E96.0"),sQuery(id+"F24.wireOp",EDGE,"E96.1")])]});
            var Q4;
            Q4=makeQuery(id+"F27.opExtrude","SWEPT_EDGE",EDGE,{"disambiguationData":[OSD([sQuery(id+"F26.wireOp",EDGE,"E103.0"),sQuery(id+"F26.wireOp",EDGE,"E103.1")])]});
            var Q5;
            Q5=makeQuery(id+"F27.opExtrude","SWEPT_EDGE",EDGE,{"disambiguationData":[OSD([sQuery(id+"F26.wireOp",EDGE,"E103.0"),sQuery(id+"F26.wireOp",EDGE,"E103.3")])]});
            var Q6;
            Q6=makeQuery(id+"F25.opExtrude","SWEPT_EDGE",EDGE,{"disambiguationData":[OSD([sQuery(id+"F24.wireOp",EDGE,"E97.0"),sQuery(id+"F24.wireOp",EDGE,"E97.3")])]});
            var Q7;
            Q7=makeQuery(id+"F25.opExtrude","SWEPT_EDGE",EDGE,{"disambiguationData":[OSD([sQuery(id+"F24.wireOp",EDGE,"E97.0"),sQuery(id+"F24.wireOp",EDGE,"E97.1")])]});
            fillet(context, id + "F40", {"entities" : qUnion([Q0, Q1, Q2, Q3, Q4, Q5, Q6, Q7]), "radius" : 1 * mm, "tangentPropagation" : true, "allowEdgeOverflow" : false});
        }
        {
            var Q0;
            {var subQ0=sQuery(id+"F26.wireOp",EDGE,"E103.3");var subQ1=sQuery(id+"F26.wireOp",EDGE,"E103.2");var subQ2=sQuery(id+"F26.wireOp",EDGE,"E103.1");var subQ3=sQuery(id+"F26.wireOp",EDGE,"E103.0");var subQ4=sQuery(id+"F26.wireOp",EDGE,"E102.0");var subQ5=sQuery(id+"F26.wireOp",EDGE,"E100.0");var subQ6=sQuery(id+"F26.wireOp",EDGE,"E99.0");var subQ7=sQuery(id+"F26.wireOp",EDGE,"E98.0");var subQ8=sQuery(id+"F22.wireOp",EDGE,"E87.right");Q0=makeQuery(id+"F28.boolean.opBoolean","MERGE",EDGE,{"derivedFrom":[makeQuery(id+"F27.boolean.opBoolean","INTERSECT",EDGE,{"derivedFrom":[makeQuery(id+"F23.boolean.opBoolean","COPY",FACE,{"derivedFrom":makeQuery(id+"F23.opExtrude","SWEPT_FACE",FACE,{"disambiguationData":[OSD([subQ8])]})}),makeQuery(id+"F27.opExtrude","CAP_FACE",FACE,{"disambiguationData":[OSD([subQ7,subQ6,subQ5,subQ4,subQ3,subQ2,subQ1,subQ0])],"isStart":false})]}),makeQuery(id+"F28.opExtrude","SWEPT_EDGE",EDGE,{"disambiguationData":[OSD([subQ8,subQ7,subQ6,subQ5,subQ4,subQ3,subQ2,subQ1,subQ0])]})]});}
            var Q1;
            {var subQ0=sQuery(id+"F22.wireOp",EDGE,"E87.right");var subQ1=sQuery(id+"F18.wireOp",EDGE,"E81.right");Q1=makeQuery(id+"F29.boolean.opBoolean","MERGE",EDGE,{"derivedFrom":[makeQuery(id+"F25.boolean.opBoolean","INTERSECT",EDGE,{"derivedFrom":[makeQuery(id+"F23.boolean.opBoolean","COPY",FACE,{"derivedFrom":makeQuery(id+"F23.opExtrude","SWEPT_FACE",FACE,{"disambiguationData":[OSD([subQ0])]})}),makeQuery(id+"F25.opExtrude","CAP_FACE",FACE,{"disambiguationData":[OSD([subQ1]),OD(0.0)],"isStart":false})]}),makeQuery(id+"F29.opExtrude","SWEPT_EDGE",EDGE,{"disambiguationData":[OSD([subQ1,subQ0,sQuery(id+"F24.wireOp",EDGE,"E97.2")])]})]});}
            var Q2;
            Q2=makeQuery(id+"F8.opExtrude","SWEPT_EDGE",EDGE,{"disambiguationData":[OSD([sQuery(id+"F0.wireOp",EDGE,"E13"),sQuery(id+"F7.wireOp",EDGE,"E35"),sQuery(id+"F7.wireOp",EDGE,"E40")])]});
            var Q3;
            Q3=makeQuery(id+"F8.opExtrude","SWEPT_EDGE",EDGE,{"disambiguationData":[OSD([sQuery(id+"F0.wireOp",EDGE,"E13"),sQuery(id+"F7.wireOp",EDGE,"E32"),sQuery(id+"F7.wireOp",EDGE,"E33")])]});
            var Q4;
            Q4=makeQuery(id+"F31.opExtrude","SWEPT_EDGE",EDGE,{"disambiguationData":[OSD([sQuery(id+"F0.wireOp",EDGE,"E8"),sQuery(id+"F0.wireOp",EDGE,"E9"),sQuery(id+"F0.wireOp",EDGE,"E10"),sQuery(id+"F0.wireOp",EDGE,"E11"),sQuery(id+"F0.wireOp",EDGE,"E12"),sQuery(id+"F0.wireOp",EDGE,"E13"),sQuery(id+"F0.wireOp",EDGE,"E14"),sQuery(id+"F0.wireOp",EDGE,"E15"),sQuery(id+"F0.wireOp",EDGE,"E16"),sQuery(id+"F0.wireOp",EDGE,"E17"),sQuery(id+"F0.wireOp",EDGE,"E18"),sQuery(id+"F0.wireOp",EDGE,"E19"),sQuery(id+"F0.wireOp",EDGE,"E20"),sQuery(id+"F0.wireOp",EDGE,"E21"),sQuery(id+"F0.wireOp",EDGE,"E22"),sQuery(id+"F0.wireOp",EDGE,"E23"),sQuery(id+"F2.wireOp",EDGE,"E24.0"),sQuery(id+"F2.wireOp",EDGE,"E24.1"),sQuery(id+"F7.wireOp",EDGE,"E29"),sQuery(id+"F7.wireOp",EDGE,"E30"),sQuery(id+"F7.wireOp",EDGE,"E31"),sQuery(id+"F7.wireOp",EDGE,"E32"),sQuery(id+"F7.wireOp",EDGE,"E33"),sQuery(id+"F7.wireOp",EDGE,"E34"),sQuery(id+"F7.wireOp",EDGE,"E35"),sQuery(id+"F7.wireOp",EDGE,"E36"),sQuery(id+"F7.wireOp",EDGE,"E37"),sQuery(id+"F7.wireOp",EDGE,"E38"),sQuery(id+"F7.wireOp",EDGE,"E39"),sQuery(id+"F7.wireOp",EDGE,"E40"),sQuery(id+"F11.wireOp",EDGE,"E72"),sQuery(id+"F30.wireOp",EDGE,"E115"),sQuery(id+"F30.wireOp",EDGE,"E116")])]});
            var Q5;
            Q5=makeQuery(id+"F31.opExtrude","SWEPT_EDGE",EDGE,{"disambiguationData":[OSD([sQuery(id+"F0.wireOp",EDGE,"E8"),sQuery(id+"F0.wireOp",EDGE,"E9"),sQuery(id+"F0.wireOp",EDGE,"E10"),sQuery(id+"F0.wireOp",EDGE,"E11"),sQuery(id+"F0.wireOp",EDGE,"E12"),sQuery(id+"F0.wireOp",EDGE,"E13"),sQuery(id+"F0.wireOp",EDGE,"E14"),sQuery(id+"F0.wireOp",EDGE,"E15"),sQuery(id+"F0.wireOp",EDGE,"E16"),sQuery(id+"F0.wireOp",EDGE,"E17"),sQuery(id+"F0.wireOp",EDGE,"E18"),sQuery(id+"F0.wireOp",EDGE,"E19"),sQuery(id+"F0.wireOp",EDGE,"E20"),sQuery(id+"F0.wireOp",EDGE,"E21"),sQuery(id+"F0.wireOp",EDGE,"E22"),sQuery(id+"F0.wireOp",EDGE,"E23"),sQuery(id+"F2.wireOp",EDGE,"E24.0"),sQuery(id+"F2.wireOp",EDGE,"E24.1"),sQuery(id+"F7.wireOp",EDGE,"E29"),sQuery(id+"F7.wireOp",EDGE,"E30"),sQuery(id+"F7.wireOp",EDGE,"E31"),sQuery(id+"F7.wireOp",EDGE,"E32"),sQuery(id+"F7.wireOp",EDGE,"E33"),sQuery(id+"F7.wireOp",EDGE,"E34"),sQuery(id+"F7.wireOp",EDGE,"E35"),sQuery(id+"F7.wireOp",EDGE,"E36"),sQuery(id+"F7.wireOp",EDGE,"E37"),sQuery(id+"F7.wireOp",EDGE,"E38"),sQuery(id+"F7.wireOp",EDGE,"E39"),sQuery(id+"F7.wireOp",EDGE,"E40"),sQuery(id+"F11.wireOp",EDGE,"E71"),sQuery(id+"F30.wireOp",EDGE,"E114"),sQuery(id+"F30.wireOp",EDGE,"E115")])]});
            var Q6;
            Q6=makeQuery(id+"F37.boolean.opBoolean","COPY",EDGE,{"derivedFrom":makeQuery(id+"F37.opExtrude","SWEPT_EDGE",EDGE,{"disambiguationData":[OSD([sQuery(id+"F36.wireOp",EDGE,"E129.top"),sQuery(id+"F36.wireOp",EDGE,"E129.right")])]})});
            var Q7;
            Q7=makeQuery(id+"F37.boolean.opBoolean","COPY",EDGE,{"derivedFrom":makeQuery(id+"F37.opExtrude","SWEPT_EDGE",EDGE,{"disambiguationData":[OSD([sQuery(id+"F36.wireOp",EDGE,"E130.top"),sQuery(id+"F36.wireOp",EDGE,"E130.right")])]})});
            fillet(context, id + "F41", {"entities" : qUnion([Q0, Q1, Q2, Q3, Q4, Q5, Q6, Q7]), "radius" : 5 * mm, "tangentPropagation" : true, "allowEdgeOverflow" : false});
        }
        {
            var Q0;
            {var subQ0=sQuery(id+"F18.wireOp",EDGE,"E81.right");Q0=makeQuery(id+"F29.boolean.opBoolean","MERGE",FACE,{"derivedFrom":[makeQuery(id+"F25.boolean.opBoolean","MERGE",FACE,{"derivedFrom":[makeQuery(id+"F1.opExtrude","SWEPT_FACE",FACE,{"disambiguationData":[OSD([sQuery(id+"F0.wireOp",EDGE,"E21")])]}),makeQuery(id+"F19.opExtrude","SWEPT_FACE",FACE,{"disambiguationData":[OSD([subQ0])]}),makeQuery(id+"F25.opExtrude","CAP_FACE",FACE,{"disambiguationData":[OSD([subQ0]),OD(0.0)],"isStart":false})]}),makeQuery(id+"F29.opExtrude","SWEPT_FACE",FACE,{"disambiguationData":[OSD([subQ0,sQuery(id+"F24.wireOp",EDGE,"E97.2")])]})]});}
            var sketch = newSketch(context, id + "F42", { "sketchPlane" : qUnion([Q0])});
            skLineSegment(sketch, "E133", {"start": v(3, 10) * mm, "end": v(-0.5, 7) * mm});
            skLineSegment(sketch, "E134", {"start": v(-0.5, 7) * mm, "end": v(3, 7) * mm});
            skLineSegment(sketch, "E135", {"start": v(3, 7) * mm, "end": v(3, 10) * mm});
            skSolve(sketch);
        }
        {
            var Q0;
            Q0 = qSketchRegion(id + "F42", true);
            var Q1;
            {var subQ0=sQuery(id+"F26.wireOp",EDGE,"E103.2");Q1=makeQuery(id+"F28.boolean.opBoolean","MERGE",FACE,{"derivedFrom":[makeQuery(id+"F27.boolean.opBoolean","MERGE",FACE,{"derivedFrom":[makeQuery(id+"F1.opExtrude","SWEPT_FACE",FACE,{"disambiguationData":[OSD([sQuery(id+"F0.wireOp",EDGE,"E17")])]}),makeQuery(id+"F19.opExtrude","SWEPT_FACE",FACE,{"disambiguationData":[OSD([sQuery(id+"F18.wireOp",EDGE,"E82.right")])]}),makeQuery(id+"F27.opExtrude","CAP_FACE",FACE,{"disambiguationData":[OSD([sQuery(id+"F26.wireOp",EDGE,"E98.0"),sQuery(id+"F26.wireOp",EDGE,"E99.0"),sQuery(id+"F26.wireOp",EDGE,"E100.0"),sQuery(id+"F26.wireOp",EDGE,"E102.0"),sQuery(id+"F26.wireOp",EDGE,"E103.0"),sQuery(id+"F26.wireOp",EDGE,"E103.1"),subQ0,sQuery(id+"F26.wireOp",EDGE,"E103.3")])],"isStart":false})]}),makeQuery(id+"F28.opExtrude","SWEPT_FACE",FACE,{"disambiguationData":[OSD([subQ0]),TDD([makeQuery(id+"F27.opExtrude","CAP_EDGE",EDGE,{"disambiguationData":[OSD([subQ0])],"isStart":false})])]})]});}
            extrude(context, id + "F43", {"entities" : qUnion([Q0]), "operationType" : NewBodyOperationType.REMOVE, "endBound" : BoundingType.UP_TO_SURFACE, "depth" : 25 * mm, "endBoundEntityFace" : qUnion([Q1]), "offsetDistance" : 25 * mm});
        }
        {
            var Q0;
            Q0=makeQuery(id+"F43.boolean.opBoolean","COPY",EDGE,{"derivedFrom":makeQuery(id+"F43.opExtrude","CAP_EDGE",EDGE,{"disambiguationData":[OSD([sQuery(id+"F42.wireOp",EDGE,"E133")])],"isStart":true})});
            var Q1;
            {var subQ0=sQuery(id+"F26.wireOp",EDGE,"E103.2");Q1=makeQuery(id+"F43.boolean.opBoolean","COPY",EDGE,{"derivedFrom":makeQuery(id+"F43.opExtrude","TWEAK_EDGE",EDGE,{"derivedFrom":[makeQuery(id+"F28.boolean.opBoolean","MERGE",FACE,{"derivedFrom":[makeQuery(id+"F27.boolean.opBoolean","MERGE",FACE,{"derivedFrom":[makeQuery(id+"F1.opExtrude","SWEPT_FACE",FACE,{"disambiguationData":[OSD([sQuery(id+"F0.wireOp",EDGE,"E17")])]}),makeQuery(id+"F19.opExtrude","SWEPT_FACE",FACE,{"disambiguationData":[OSD([sQuery(id+"F18.wireOp",EDGE,"E82.right")])]}),makeQuery(id+"F27.opExtrude","CAP_FACE",FACE,{"disambiguationData":[OSD([sQuery(id+"F26.wireOp",EDGE,"E98.0"),sQuery(id+"F26.wireOp",EDGE,"E99.0"),sQuery(id+"F26.wireOp",EDGE,"E100.0"),sQuery(id+"F26.wireOp",EDGE,"E102.0"),sQuery(id+"F26.wireOp",EDGE,"E103.0"),sQuery(id+"F26.wireOp",EDGE,"E103.1"),subQ0,sQuery(id+"F26.wireOp",EDGE,"E103.3")])],"isStart":false})]}),makeQuery(id+"F28.opExtrude","SWEPT_FACE",FACE,{"disambiguationData":[OSD([subQ0]),TDD([makeQuery(id+"F27.opExtrude","CAP_EDGE",EDGE,{"disambiguationData":[OSD([subQ0])],"isStart":false})])]})]}),makeQuery(id+"F42.imprint","IMPRINT",EDGE,{"derivedFrom":sQuery(id+"F42.wireOp",EDGE,"E133")})]})});}
            fillet(context, id + "F44", {"entities" : qUnion([Q0, Q1]), "radius" : 4 * mm, "tangentPropagation" : true, "allowEdgeOverflow" : false});
        }
        {
            var Q0;
            {var subQ0=sQuery(id+"F11.wireOp",EDGE,"E71");var subQ1=makeQuery(id+"F12.opExtrude","SWEPT_FACE",FACE,{"disambiguationData":[OSD([subQ0])]});var subQ2=sQuery(id+"F18.wireOp",EDGE,"E79.right");var subQ3=makeQuery(id+"F19.opExtrude","SWEPT_FACE",FACE,{"disambiguationData":[OSD([subQ2])]});var subQ4=makeQuery(id+"F10.opExtrude","SWEPT_FACE",FACE,{"disambiguationData":[OSD([sQuery(id+"F9.wireOp",EDGE,"E51.1"),sQuery(id+"F9.wireOp",EDGE,"E54")])]});var subQ5=sQuery(id+"F0.wireOp",EDGE,"E23");var subQ6=sQuery(id+"F0.wireOp",EDGE,"E22");var subQ7=sQuery(id+"F0.wireOp",EDGE,"E21");var subQ8=sQuery(id+"F0.wireOp",EDGE,"E20");var subQ9=sQuery(id+"F0.wireOp",EDGE,"E19");var subQ10=sQuery(id+"F0.wireOp",EDGE,"E18");var subQ11=sQuery(id+"F0.wireOp",EDGE,"E17");var subQ12=sQuery(id+"F0.wireOp",EDGE,"E16");var subQ13=sQuery(id+"F0.wireOp",EDGE,"E15");var subQ14=sQuery(id+"F0.wireOp",EDGE,"E14");var subQ15=sQuery(id+"F0.wireOp",EDGE,"E13");var subQ16=sQuery(id+"F0.wireOp",EDGE,"E12");var subQ17=sQuery(id+"F0.wireOp",EDGE,"E11");var subQ18=sQuery(id+"F0.wireOp",EDGE,"E10");var subQ19=sQuery(id+"F0.wireOp",EDGE,"E9");var subQ20=sQuery(id+"F0.wireOp",EDGE,"E8");var subQ21=makeQuery(id+"F8.opExtrude","CAP_FACE",FACE,{"disambiguationData":[OSD([subQ20,subQ19,subQ18,subQ17,subQ16,subQ15,subQ14,subQ13,subQ12,subQ11,subQ10,subQ9,subQ8,subQ7,subQ6,subQ5]),OD(1.0)],"isStart":false});var subQ22=makeQuery(id+"F8.opExtrude","CAP_FACE",FACE,{"disambiguationData":[OSD([subQ20,subQ19,subQ18,subQ17,subQ16,subQ15,subQ14,subQ13,subQ12,subQ11,subQ10,subQ9,subQ8,subQ7,subQ6,subQ5]),OD(0.0)],"isStart":false});var subQ23=makeQuery(id+"F1.opExtrude","CAP_FACE",FACE,{"disambiguationData":[OSD([subQ20,subQ19,subQ18,subQ17,subQ16,subQ15,subQ14,subQ13,subQ12,subQ11,subQ10,subQ9,subQ8,subQ7,subQ6,subQ5])],"isStart":false});var subQ24=makeQuery(id+"F1.opExtrude","SWEPT_FACE",FACE,{"disambiguationData":[OSD([subQ8])]});var subQ25=sQuery(id+"F11.wireOp",EDGE,"E70");var subQ26=sQuery(id+"F11.wireOp",EDGE,"E60");var subQ27=makeQuery(id+"F12.opExtrude","CAP_FACE",FACE,{"disambiguationData":[OSD([subQ26,sQuery(id+"F11.wireOp",EDGE,"E62"),sQuery(id+"F11.wireOp",EDGE,"E64"),sQuery(id+"F11.wireOp",EDGE,"E65"),subQ25,subQ0,sQuery(id+"F11.wireOp",EDGE,"E72"),sQuery(id+"F11.wireOp",EDGE,"E73")])],"isStart":true});var subQ28=makeQuery(id+"F1.opExtrude","SWEPT_FACE",FACE,{"disambiguationData":[OSD([subQ6])]});var subQ29=sQuery(id+"F2.wireOp",EDGE,"E24.0");var subQ30=makeQuery(id+"F10.opExtrude","CAP_FACE",FACE,{"disambiguationData":[OSD([subQ29]),OD(2.0)],"isStart":false});var subQ31=sQuery(id+"F2.wireOp",EDGE,"E24.2");var subQ32=makeQuery(id+"F3.opExtrude","CAP_FACE",FACE,{"disambiguationData":[OSD([subQ31])],"isStart":false});var subQ33=sQuery(id+"F18.wireOp",EDGE,"E79.left");var subQ34=sQuery(id+"F18.wireOp",EDGE,"E79.top");var subQ35=makeQuery(id+"F19.opExtrude","CAP_FACE",FACE,{"disambiguationData":[OSD([sQuery(id+"F18.wireOp",EDGE,"E79.bottom"),subQ34,subQ33,subQ2])],"isStart":true});var subQ36=makeQuery(id+"F21.opExtrude","SWEPT_FACE",FACE,{"disambiguationData":[OSD([sQuery(id+"F20.wireOp",EDGE,"E83.top")])]});var subQ38=makeQuery(id+"F21.opExtrude","SWEPT_FACE",FACE,{"disambiguationData":[OSD([sQuery(id+"F20.wireOp",EDGE,"E83.bottom")])]});var subQ39=sQuery(id+"F30.wireOp",EDGE,"E115");var subQ40=makeQuery(id+"F25.opExtrude","CAP_FACE",FACE,{"disambiguationData":[OSD([sQuery(id+"F18.wireOp",EDGE,"E81.right")]),OD(1.0)],"isStart":false});var subQ41=makeQuery(id+"F19.boolean.opBoolean","MERGE",FACE,{"derivedFrom":[makeQuery(id+"F12.boolean.opBoolean","MERGE",FACE,{"derivedFrom":[subQ24,subQ1]}),subQ3]});Q0=makeQuery(id+"F39.boolean.opBoolean","MERGE",FACE,{"derivedFrom":[makeQuery(id+"F31.boolean.opBoolean","SPLIT",FACE,{"disambiguationData":[TD([subQ23,subQ24,subQ28,subQ32,subQ22,subQ21,subQ4,subQ30,subQ27,subQ1,subQ35,subQ3,subQ36,makeQuery(id+"F21.boolean.opBoolean","COPY",FACE,{"disambiguationData":[TD([makeQuery(id+"F1.opExtrude","SWEPT_FACE",FACE,{"disambiguationData":[OSD([subQ19])]})])],"derivedFrom":subQ38}),makeQuery(id+"F25.opExtrude","SWEPT_FACE",FACE,{"disambiguationData":[OSD([sQuery(id+"F24.wireOp",EDGE,"E92.0")])]}),makeQuery(id+"F25.opExtrude","SWEPT_FACE",FACE,{"disambiguationData":[OSD([sQuery(id+"F24.wireOp",EDGE,"E93.0")])]}),makeQuery(id+"F25.opExtrude","SWEPT_FACE",FACE,{"disambiguationData":[OSD([sQuery(id+"F24.wireOp",EDGE,"E96.0")])]}),makeQuery(id+"F25.opExtrude","SWEPT_FACE",FACE,{"disambiguationData":[OSD([sQuery(id+"F24.wireOp",EDGE,"E96.1")])]}),makeQuery(id+"F25.opExtrude","SWEPT_FACE",FACE,{"disambiguationData":[OSD([sQuery(id+"F24.wireOp",EDGE,"E96.3")])]}),subQ40,makeQuery(id+"F31.opExtrude","CAP_FACE",FACE,{"disambiguationData":[OSD([sQuery(id+"F30.wireOp",EDGE,"E109"),sQuery(id+"F30.wireOp",EDGE,"E110"),sQuery(id+"F30.wireOp",EDGE,"E111"),sQuery(id+"F30.wireOp",EDGE,"E112"),sQuery(id+"F30.wireOp",EDGE,"E113"),sQuery(id+"F30.wireOp",EDGE,"E114"),subQ39,sQuery(id+"F30.wireOp",EDGE,"E116")])],"isStart":false}),makeQuery(id+"F31.opExtrude","SWEPT_FACE",FACE,{"disambiguationData":[OSD([subQ39])]})])],"derivedFrom":makeQuery(id+"F25.boolean.opBoolean","MERGE",FACE,{"derivedFrom":[makeQuery(id+"F21.boolean.opBoolean","SPLIT",FACE,{"disambiguationData":[TD([makeQuery(id+"F3.opExtrude","CAP_FACE",FACE,{"disambiguationData":[OSD([subQ29])],"isStart":true})])],"derivedFrom":subQ41}),makeQuery(id+"F21.boolean.opBoolean","SPLIT",FACE,{"disambiguationData":[TD([subQ32])],"derivedFrom":subQ41}),subQ40]})}),makeQuery(id+"F39.opExtrude","SWEPT_FACE",FACE,{"disambiguationData":[OSD([sQuery(id+"F38.wireOp",EDGE,"E132.left")])]})]});}
            var sketch = newSketch(context, id + "F45", { "sketchPlane" : qUnion([Q0])});
            skLineSegment(sketch, "E136", {"start": v(-60, 7) * mm, "end": v(-61, 10) * mm});
            skLineSegment(sketch, "E137", {"start": v(-61, 10) * mm, "end": v(-61, 7) * mm});
            skLineSegment(sketch, "E138", {"start": v(-61, 7) * mm, "end": v(-60, 7) * mm});
            skSolve(sketch);
        }
        {
            var Q0;
            Q0 = qSketchRegion(id + "F45", true);
            var Q1;
            {var subQ0=sQuery(id+"F11.wireOp",EDGE,"E72");var subQ1=makeQuery(id+"F12.opExtrude","SWEPT_FACE",FACE,{"disambiguationData":[OSD([subQ0])]});var subQ2=sQuery(id+"F26.wireOp",EDGE,"E108.3");var subQ3=sQuery(id+"F11.wireOp",EDGE,"E73");var subQ4=sQuery(id+"F11.wireOp",EDGE,"E60");var subQ5=makeQuery(id+"F12.opExtrude","CAP_FACE",FACE,{"disambiguationData":[OSD([subQ4,sQuery(id+"F11.wireOp",EDGE,"E62"),sQuery(id+"F11.wireOp",EDGE,"E64"),sQuery(id+"F11.wireOp",EDGE,"E65"),sQuery(id+"F11.wireOp",EDGE,"E70"),sQuery(id+"F11.wireOp",EDGE,"E71"),subQ0,subQ3])],"isStart":true});var subQ6=sQuery(id+"F26.wireOp",EDGE,"E105.0");var subQ7=makeQuery(id+"F10.opExtrude","SWEPT_FACE",FACE,{"disambiguationData":[OSD([sQuery(id+"F9.wireOp",EDGE,"E56.0"),sQuery(id+"F9.wireOp",EDGE,"E57")])]});var subQ8=makeQuery(id+"F21.opExtrude","SWEPT_FACE",FACE,{"disambiguationData":[OSD([sQuery(id+"F20.wireOp",EDGE,"E83.top")])]});var subQ9=sQuery(id+"F0.wireOp",EDGE,"E23");var subQ10=sQuery(id+"F0.wireOp",EDGE,"E22");var subQ11=sQuery(id+"F0.wireOp",EDGE,"E21");var subQ12=sQuery(id+"F0.wireOp",EDGE,"E20");var subQ13=sQuery(id+"F0.wireOp",EDGE,"E19");var subQ14=sQuery(id+"F0.wireOp",EDGE,"E18");var subQ15=sQuery(id+"F0.wireOp",EDGE,"E17");var subQ16=sQuery(id+"F0.wireOp",EDGE,"E16");var subQ17=sQuery(id+"F0.wireOp",EDGE,"E15");var subQ18=sQuery(id+"F0.wireOp",EDGE,"E14");var subQ19=sQuery(id+"F0.wireOp",EDGE,"E13");var subQ20=sQuery(id+"F0.wireOp",EDGE,"E12");var subQ21=sQuery(id+"F0.wireOp",EDGE,"E11");var subQ22=sQuery(id+"F0.wireOp",EDGE,"E10");var subQ23=sQuery(id+"F0.wireOp",EDGE,"E9");var subQ24=sQuery(id+"F0.wireOp",EDGE,"E8");var subQ25=makeQuery(id+"F8.opExtrude","CAP_FACE",FACE,{"disambiguationData":[OSD([subQ24,subQ23,subQ22,subQ21,subQ20,subQ19,subQ18,subQ17,subQ16,subQ15,subQ14,subQ13,subQ12,subQ11,subQ10,subQ9]),OD(0.0)],"isStart":false});var subQ26=sQuery(id+"F18.wireOp",EDGE,"E80.right");var subQ27=makeQuery(id+"F19.opExtrude","SWEPT_FACE",FACE,{"disambiguationData":[OSD([subQ26])]});var subQ28=sQuery(id+"F2.wireOp",EDGE,"E24.3");var subQ29=makeQuery(id+"F1.opExtrude","SWEPT_FACE",FACE,{"disambiguationData":[OSD([subQ16])]});var subQ30=makeQuery(id+"F1.opExtrude","SWEPT_FACE",FACE,{"disambiguationData":[OSD([subQ18])]});var subQ31=sQuery(id+"F18.wireOp",EDGE,"E80.left");var subQ32=sQuery(id+"F18.wireOp",EDGE,"E80.top");var subQ34=makeQuery(id+"F21.opExtrude","SWEPT_FACE",FACE,{"disambiguationData":[OSD([sQuery(id+"F20.wireOp",EDGE,"E83.bottom")])]});var subQ35=makeQuery(id+"F1.opExtrude","CAP_FACE",FACE,{"disambiguationData":[OSD([subQ24,subQ23,subQ22,subQ21,subQ20,subQ19,subQ18,subQ17,subQ16,subQ15,subQ14,subQ13,subQ12,subQ11,subQ10,subQ9])],"isStart":false});var subQ36=sQuery(id+"F26.wireOp",EDGE,"E108.1");var subQ37=makeQuery(id+"F8.opExtrude","CAP_FACE",FACE,{"disambiguationData":[OSD([subQ24,subQ23,subQ22,subQ21,subQ20,subQ19,subQ18,subQ17,subQ16,subQ15,subQ14,subQ13,subQ12,subQ11,subQ10,subQ9]),OD(1.0)],"isStart":false});var subQ38=sQuery(id+"F2.wireOp",EDGE,"E24.0");var subQ39=makeQuery(id+"F10.opExtrude","CAP_FACE",FACE,{"disambiguationData":[OSD([subQ38]),OD(3.0)],"isStart":false});var subQ40=makeQuery(id+"F3.opExtrude","CAP_FACE",FACE,{"disambiguationData":[OSD([subQ28])],"isStart":false});var subQ41=makeQuery(id+"F19.opExtrude","CAP_FACE",FACE,{"disambiguationData":[OSD([sQuery(id+"F18.wireOp",EDGE,"E80.bottom"),subQ32,subQ31,subQ26])],"isStart":true});var subQ42=sQuery(id+"F26.wireOp",EDGE,"E108.2");var subQ43=sQuery(id+"F26.wireOp",EDGE,"E106.0");var subQ44=makeQuery(id+"F27.opExtrude","CAP_FACE",FACE,{"disambiguationData":[OSD([sQuery(id+"F26.wireOp",EDGE,"E104.0"),subQ6,subQ43,sQuery(id+"F26.wireOp",EDGE,"E107.0"),sQuery(id+"F26.wireOp",EDGE,"E108.0"),subQ36,subQ42,subQ2])],"isStart":false});var subQ45=sQuery(id+"F30.wireOp",EDGE,"E115");var subQ46=makeQuery(id+"F19.boolean.opBoolean","MERGE",FACE,{"derivedFrom":[makeQuery(id+"F12.boolean.opBoolean","MERGE",FACE,{"derivedFrom":[subQ29,subQ1]}),subQ27]});Q1=makeQuery(id+"F39.boolean.opBoolean","MERGE",FACE,{"derivedFrom":[makeQuery(id+"F31.boolean.opBoolean","SPLIT",FACE,{"disambiguationData":[TD([subQ35,subQ30,subQ29,subQ40,subQ25,subQ37,subQ7,subQ39,subQ5,subQ1,subQ41,subQ27,subQ8,makeQuery(id+"F21.boolean.opBoolean","COPY",FACE,{"disambiguationData":[TD([makeQuery(id+"F1.opExtrude","SWEPT_FACE",FACE,{"disambiguationData":[OSD([subQ21])]})])],"derivedFrom":subQ34}),subQ44,makeQuery(id+"F27.opExtrude","SWEPT_FACE",FACE,{"disambiguationData":[OSD([subQ6])]}),makeQuery(id+"F27.opExtrude","SWEPT_FACE",FACE,{"disambiguationData":[OSD([subQ43])]}),makeQuery(id+"F27.opExtrude","SWEPT_FACE",FACE,{"disambiguationData":[OSD([subQ36])]}),makeQuery(id+"F27.opExtrude","SWEPT_FACE",FACE,{"disambiguationData":[OSD([subQ42])]}),makeQuery(id+"F27.opExtrude","SWEPT_FACE",FACE,{"disambiguationData":[OSD([subQ2])]}),makeQuery(id+"F31.opExtrude","CAP_FACE",FACE,{"disambiguationData":[OSD([sQuery(id+"F30.wireOp",EDGE,"E109"),sQuery(id+"F30.wireOp",EDGE,"E110"),sQuery(id+"F30.wireOp",EDGE,"E111"),sQuery(id+"F30.wireOp",EDGE,"E112"),sQuery(id+"F30.wireOp",EDGE,"E113"),sQuery(id+"F30.wireOp",EDGE,"E114"),subQ45,sQuery(id+"F30.wireOp",EDGE,"E116")])],"isStart":false}),makeQuery(id+"F31.opExtrude","SWEPT_FACE",FACE,{"disambiguationData":[OSD([subQ45])]})])],"derivedFrom":makeQuery(id+"F27.boolean.opBoolean","MERGE",FACE,{"derivedFrom":[makeQuery(id+"F21.boolean.opBoolean","SPLIT",FACE,{"disambiguationData":[TD([makeQuery(id+"F3.opExtrude","CAP_FACE",FACE,{"disambiguationData":[OSD([subQ38])],"isStart":true})])],"derivedFrom":subQ46}),makeQuery(id+"F21.boolean.opBoolean","SPLIT",FACE,{"disambiguationData":[TD([subQ40])],"derivedFrom":subQ46}),subQ44]})}),makeQuery(id+"F39.opExtrude","SWEPT_FACE",FACE,{"disambiguationData":[OSD([sQuery(id+"F38.wireOp",EDGE,"E131.left")])]})]});}
            extrude(context, id + "F46", {"entities" : qUnion([Q0]), "operationType" : NewBodyOperationType.REMOVE, "endBound" : BoundingType.UP_TO_SURFACE, "depth" : 25 * mm, "endBoundEntityFace" : qUnion([Q1]), "offsetDistance" : 25 * mm});
        }
        {
            var Q0;
            {var subQ19=makeQuery(id+"F14.opExtrude","SWEPT_FACE",FACE,{"disambiguationData":[OSD([sQuery(id+"F13.wireOp",EDGE,"E74.top")])]});var subQ20=sQuery(id+"F11.wireOp",EDGE,"E60");var subQ21=makeQuery(id+"F12.opExtrude","SWEPT_FACE",FACE,{"disambiguationData":[OSD([subQ20])]});Q0=makeQuery(id+"F35.boolean.opBoolean","MERGE",FACE,{"derivedFrom":[makeQuery(id+"F31.boolean.opBoolean","SPLIT",FACE,{"disambiguationData":[TD([makeQuery(id+"F16.boolean.opBoolean","COPY",FACE,{"derivedFrom":makeQuery(id+"F16.opExtrude","SWEPT_FACE",FACE,{"disambiguationData":[OSD([sQuery(id+"F15.wireOp",EDGE,"E76")])]})})])],"derivedFrom":makeQuery(id+"F14.boolean.opBoolean","MERGE",FACE,{"derivedFrom":[subQ21,subQ19]})}),makeQuery(id+"F35.opExtrude","SWEPT_FACE",FACE,{"disambiguationData":[OSD([sQuery(id+"F34.wireOp",EDGE,"E126")])]})]});}
            extrude(context, id + "F47", {"entities" : qUnion([Q0]), "operationType" : NewBodyOperationType.REMOVE, "oppositeDirection" : true, "depth" : 3 * mm, "offsetDistance" : 25 * mm});
        }
        {
            var Q0;
            {var subQ1=sQuery(id+"F30.wireOp",EDGE,"E111");Q0=makeQuery(id+"F47.boolean.opBoolean","COPY",EDGE,{"derivedFrom":makeQuery(id+"F47.opExtrude","CAP_EDGE",EDGE,{"disambiguationData":[OSD([subQ1]),TDD([makeQuery(id+"F35.boolean.opBoolean","SPLIT",EDGE,{"disambiguationData":[TD([makeQuery(id+"F14.opExtrude","SWEPT_FACE",FACE,{"disambiguationData":[OSD([sQuery(id+"F13.wireOp",EDGE,"E74.left")])]})])],"derivedFrom":makeQuery(id+"F31.opExtrude","CAP_EDGE",EDGE,{"disambiguationData":[OSD([subQ1])],"isStart":false})})])],"isStart":false})});}
            var Q1;
            {var subQ1=sQuery(id+"F30.wireOp",EDGE,"E111");Q1=makeQuery(id+"F47.boolean.opBoolean","COPY",EDGE,{"derivedFrom":makeQuery(id+"F47.opExtrude","CAP_EDGE",EDGE,{"disambiguationData":[OSD([subQ1]),TDD([makeQuery(id+"F35.boolean.opBoolean","SPLIT",EDGE,{"disambiguationData":[TD([makeQuery(id+"F14.opExtrude","SWEPT_FACE",FACE,{"disambiguationData":[OSD([sQuery(id+"F13.wireOp",EDGE,"E74.right")])]})])],"derivedFrom":makeQuery(id+"F31.opExtrude","CAP_EDGE",EDGE,{"disambiguationData":[OSD([subQ1])],"isStart":false})})])],"isStart":false})});}
            var Q2;
            Q2=makeQuery(id+"F47.boolean.opBoolean","COPY",EDGE,{"derivedFrom":makeQuery(id+"F47.opExtrude","CAP_EDGE",EDGE,{"disambiguationData":[OSD([sQuery(id+"F30.wireOp",EDGE,"E111"),sQuery(id+"F34.wireOp",EDGE,"E125"),sQuery(id+"F34.wireOp",EDGE,"E126")])],"isStart":false})});
            var Q3;
            Q3=makeQuery(id+"F47.boolean.opBoolean","COPY",EDGE,{"derivedFrom":makeQuery(id+"F47.opExtrude","CAP_EDGE",EDGE,{"disambiguationData":[OSD([sQuery(id+"F30.wireOp",EDGE,"E111"),sQuery(id+"F34.wireOp",EDGE,"E126"),sQuery(id+"F34.wireOp",EDGE,"E127")])],"isStart":false})});
            fillet(context, id + "F48", {"entities" : qUnion([Q0, Q1, Q2, Q3]), "radius" : 1 * mm, "tangentPropagation" : true, "allowEdgeOverflow" : false});
        }
        {
            var Q0;
            Q0=makeQuery(id+"F16.boolean.opBoolean","INTERSECT",EDGE,{"derivedFrom":[makeQuery(id+"F14.boolean.opBoolean","MERGE",FACE,{"derivedFrom":[makeQuery(id+"F12.opExtrude","SWEPT_FACE",FACE,{"disambiguationData":[OSD([sQuery(id+"F11.wireOp",EDGE,"E62")])]}),makeQuery(id+"F14.opExtrude","SWEPT_FACE",FACE,{"disambiguationData":[OSD([sQuery(id+"F13.wireOp",EDGE,"E74.bottom")])]})]}),makeQuery(id+"F16.opExtrude","SWEPT_FACE",FACE,{"disambiguationData":[OSD([sQuery(id+"F15.wireOp",EDGE,"E76")])]})]});
            var Q1;
            Q1=makeQuery(id+"F27.boolean.opBoolean","MERGE",EDGE,{"derivedFrom":[makeQuery(id+"F21.boolean.opBoolean","INTERSECT",EDGE,{"derivedFrom":[makeQuery(id+"F19.boolean.opBoolean","MERGE",FACE,{"derivedFrom":[makeQuery(id+"F12.boolean.opBoolean","MERGE",FACE,{"derivedFrom":[makeQuery(id+"F10.boolean.opBoolean","MERGE",FACE,{"derivedFrom":[makeQuery(id+"F1.opExtrude","SWEPT_FACE",FACE,{"disambiguationData":[OSD([sQuery(id+"F0.wireOp",EDGE,"E11")])]}),makeQuery(id+"F10.opExtrude","SWEPT_FACE",FACE,{"disambiguationData":[OSD([sQuery(id+"F9.wireOp",EDGE,"E43")])]}),makeQuery(id+"F10.opExtrude","SWEPT_FACE",FACE,{"disambiguationData":[OSD([sQuery(id+"F9.wireOp",EDGE,"E58")])]})]}),makeQuery(id+"F12.opExtrude","SWEPT_FACE",FACE,{"disambiguationData":[OSD([sQuery(id+"F11.wireOp",EDGE,"E73")])]})]}),makeQuery(id+"F19.opExtrude","SWEPT_FACE",FACE,{"disambiguationData":[OSD([sQuery(id+"F18.wireOp",EDGE,"E80.left")])]}),makeQuery(id+"F19.opExtrude","SWEPT_FACE",FACE,{"disambiguationData":[OSD([sQuery(id+"F18.wireOp",EDGE,"E82.left")])]})]}),makeQuery(id+"F21.opExtrude","SWEPT_FACE",FACE,{"disambiguationData":[OSD([sQuery(id+"F20.wireOp",EDGE,"E83.bottom")])]})]}),makeQuery(id+"F27.opExtrude","CAP_EDGE",EDGE,{"disambiguationData":[OSD([sQuery(id+"F26.wireOp",EDGE,"E106.0")])],"isStart":true})]});
            var Q2;
            Q2=makeQuery(id+"F21.boolean.opBoolean","INTERSECT",EDGE,{"derivedFrom":[makeQuery(id+"F19.boolean.opBoolean","MERGE",FACE,{"derivedFrom":[makeQuery(id+"F12.boolean.opBoolean","MERGE",FACE,{"derivedFrom":[makeQuery(id+"F10.boolean.opBoolean","MERGE",FACE,{"derivedFrom":[makeQuery(id+"F1.opExtrude","SWEPT_FACE",FACE,{"disambiguationData":[OSD([sQuery(id+"F0.wireOp",EDGE,"E11")])]}),makeQuery(id+"F10.opExtrude","SWEPT_FACE",FACE,{"disambiguationData":[OSD([sQuery(id+"F9.wireOp",EDGE,"E43")])]}),makeQuery(id+"F10.opExtrude","SWEPT_FACE",FACE,{"disambiguationData":[OSD([sQuery(id+"F9.wireOp",EDGE,"E58")])]})]}),makeQuery(id+"F12.opExtrude","SWEPT_FACE",FACE,{"disambiguationData":[OSD([sQuery(id+"F11.wireOp",EDGE,"E73")])]})]}),makeQuery(id+"F19.opExtrude","SWEPT_FACE",FACE,{"disambiguationData":[OSD([sQuery(id+"F18.wireOp",EDGE,"E80.left")])]}),makeQuery(id+"F19.opExtrude","SWEPT_FACE",FACE,{"disambiguationData":[OSD([sQuery(id+"F18.wireOp",EDGE,"E82.left")])]})]}),makeQuery(id+"F21.opExtrude","SWEPT_FACE",FACE,{"disambiguationData":[OSD([sQuery(id+"F20.wireOp",EDGE,"E83.right")])]})]});
            var Q3;
            {var subQ0=makeQuery(id+"F19.opExtrude","SWEPT_FACE",FACE,{"disambiguationData":[OSD([sQuery(id+"F18.wireOp",EDGE,"E82.left")])]});var subQ1=makeQuery(id+"F19.opExtrude","SWEPT_FACE",FACE,{"disambiguationData":[OSD([sQuery(id+"F18.wireOp",EDGE,"E80.left")])]});var subQ14=sQuery(id+"F0.wireOp",EDGE,"E11");var subQ19=makeQuery(id+"F10.opExtrude","SWEPT_FACE",FACE,{"disambiguationData":[OSD([sQuery(id+"F9.wireOp",EDGE,"E58")])]});var subQ21=sQuery(id+"F11.wireOp",EDGE,"E73");var subQ22=makeQuery(id+"F12.opExtrude","SWEPT_FACE",FACE,{"disambiguationData":[OSD([subQ21])]});var subQ23=makeQuery(id+"F1.opExtrude","SWEPT_FACE",FACE,{"disambiguationData":[OSD([subQ14])]});var subQ24=makeQuery(id+"F10.opExtrude","SWEPT_FACE",FACE,{"disambiguationData":[OSD([sQuery(id+"F9.wireOp",EDGE,"E43")])]});var subQ27=makeQuery(id+"F21.opExtrude","SWEPT_FACE",FACE,{"disambiguationData":[OSD([sQuery(id+"F20.wireOp",EDGE,"E83.top")])]});var subQ28=sQuery(id+"F26.wireOp",EDGE,"E105.0");Q3=makeQuery(id+"F27.boolean.opBoolean","SPLIT",EDGE,{"disambiguationData":[TD([makeQuery(id+"F27.opExtrude","SWEPT_FACE",FACE,{"disambiguationData":[OSD([subQ28])]})])],"derivedFrom":makeQuery(id+"F21.boolean.opBoolean","INTERSECT",EDGE,{"derivedFrom":[makeQuery(id+"F19.boolean.opBoolean","MERGE",FACE,{"derivedFrom":[makeQuery(id+"F12.boolean.opBoolean","MERGE",FACE,{"derivedFrom":[makeQuery(id+"F10.boolean.opBoolean","MERGE",FACE,{"derivedFrom":[subQ23,subQ24,subQ19]}),subQ22]}),subQ1,subQ0]}),subQ27]})});}
            var Q4;
            Q4=makeQuery(id+"F27.opExtrude","CAP_EDGE",EDGE,{"disambiguationData":[OSD([sQuery(id+"F26.wireOp",EDGE,"E105.0")])],"isStart":true});
            var Q5;
            Q5=makeQuery(id+"F21.boolean.opBoolean","INTERSECT",EDGE,{"derivedFrom":[makeQuery(id+"F19.boolean.opBoolean","MERGE",FACE,{"derivedFrom":[makeQuery(id+"F12.boolean.opBoolean","MERGE",FACE,{"derivedFrom":[makeQuery(id+"F10.boolean.opBoolean","MERGE",FACE,{"derivedFrom":[makeQuery(id+"F1.opExtrude","SWEPT_FACE",FACE,{"disambiguationData":[OSD([sQuery(id+"F0.wireOp",EDGE,"E11")])]}),makeQuery(id+"F10.opExtrude","SWEPT_FACE",FACE,{"disambiguationData":[OSD([sQuery(id+"F9.wireOp",EDGE,"E43")])]}),makeQuery(id+"F10.opExtrude","SWEPT_FACE",FACE,{"disambiguationData":[OSD([sQuery(id+"F9.wireOp",EDGE,"E58")])]})]}),makeQuery(id+"F12.opExtrude","SWEPT_FACE",FACE,{"disambiguationData":[OSD([sQuery(id+"F11.wireOp",EDGE,"E73")])]})]}),makeQuery(id+"F19.opExtrude","SWEPT_FACE",FACE,{"disambiguationData":[OSD([sQuery(id+"F18.wireOp",EDGE,"E80.left")])]}),makeQuery(id+"F19.opExtrude","SWEPT_FACE",FACE,{"disambiguationData":[OSD([sQuery(id+"F18.wireOp",EDGE,"E82.left")])]})]}),makeQuery(id+"F21.opExtrude","SWEPT_FACE",FACE,{"disambiguationData":[OSD([sQuery(id+"F20.wireOp",EDGE,"E85.bottom")])]})]});
            var Q6;
            Q6=makeQuery(id+"F21.boolean.opBoolean","INTERSECT",EDGE,{"derivedFrom":[makeQuery(id+"F19.boolean.opBoolean","MERGE",FACE,{"derivedFrom":[makeQuery(id+"F12.boolean.opBoolean","MERGE",FACE,{"derivedFrom":[makeQuery(id+"F10.boolean.opBoolean","MERGE",FACE,{"derivedFrom":[makeQuery(id+"F1.opExtrude","SWEPT_FACE",FACE,{"disambiguationData":[OSD([sQuery(id+"F0.wireOp",EDGE,"E11")])]}),makeQuery(id+"F10.opExtrude","SWEPT_FACE",FACE,{"disambiguationData":[OSD([sQuery(id+"F9.wireOp",EDGE,"E43")])]}),makeQuery(id+"F10.opExtrude","SWEPT_FACE",FACE,{"disambiguationData":[OSD([sQuery(id+"F9.wireOp",EDGE,"E58")])]})]}),makeQuery(id+"F12.opExtrude","SWEPT_FACE",FACE,{"disambiguationData":[OSD([sQuery(id+"F11.wireOp",EDGE,"E73")])]})]}),makeQuery(id+"F19.opExtrude","SWEPT_FACE",FACE,{"disambiguationData":[OSD([sQuery(id+"F18.wireOp",EDGE,"E80.left")])]}),makeQuery(id+"F19.opExtrude","SWEPT_FACE",FACE,{"disambiguationData":[OSD([sQuery(id+"F18.wireOp",EDGE,"E82.left")])]})]}),makeQuery(id+"F21.opExtrude","SWEPT_FACE",FACE,{"disambiguationData":[OSD([sQuery(id+"F20.wireOp",EDGE,"E85.right")])]})]});
            var Q7;
            Q7=makeQuery(id+"F21.boolean.opBoolean","INTERSECT",EDGE,{"derivedFrom":[makeQuery(id+"F19.boolean.opBoolean","MERGE",FACE,{"derivedFrom":[makeQuery(id+"F12.boolean.opBoolean","MERGE",FACE,{"derivedFrom":[makeQuery(id+"F10.boolean.opBoolean","MERGE",FACE,{"derivedFrom":[makeQuery(id+"F1.opExtrude","SWEPT_FACE",FACE,{"disambiguationData":[OSD([sQuery(id+"F0.wireOp",EDGE,"E11")])]}),makeQuery(id+"F10.opExtrude","SWEPT_FACE",FACE,{"disambiguationData":[OSD([sQuery(id+"F9.wireOp",EDGE,"E43")])]}),makeQuery(id+"F10.opExtrude","SWEPT_FACE",FACE,{"disambiguationData":[OSD([sQuery(id+"F9.wireOp",EDGE,"E58")])]})]}),makeQuery(id+"F12.opExtrude","SWEPT_FACE",FACE,{"disambiguationData":[OSD([sQuery(id+"F11.wireOp",EDGE,"E73")])]})]}),makeQuery(id+"F19.opExtrude","SWEPT_FACE",FACE,{"disambiguationData":[OSD([sQuery(id+"F18.wireOp",EDGE,"E80.left")])]}),makeQuery(id+"F19.opExtrude","SWEPT_FACE",FACE,{"disambiguationData":[OSD([sQuery(id+"F18.wireOp",EDGE,"E82.left")])]})]}),makeQuery(id+"F21.opExtrude","SWEPT_FACE",FACE,{"disambiguationData":[OSD([sQuery(id+"F20.wireOp",EDGE,"E85.top")])]})]});
            var Q8;
            Q8=makeQuery(id+"F21.boolean.opBoolean","INTERSECT",EDGE,{"derivedFrom":[makeQuery(id+"F19.boolean.opBoolean","MERGE",FACE,{"derivedFrom":[makeQuery(id+"F12.boolean.opBoolean","MERGE",FACE,{"derivedFrom":[makeQuery(id+"F10.boolean.opBoolean","MERGE",FACE,{"derivedFrom":[makeQuery(id+"F1.opExtrude","SWEPT_FACE",FACE,{"disambiguationData":[OSD([sQuery(id+"F0.wireOp",EDGE,"E11")])]}),makeQuery(id+"F10.opExtrude","SWEPT_FACE",FACE,{"disambiguationData":[OSD([sQuery(id+"F9.wireOp",EDGE,"E43")])]}),makeQuery(id+"F10.opExtrude","SWEPT_FACE",FACE,{"disambiguationData":[OSD([sQuery(id+"F9.wireOp",EDGE,"E58")])]})]}),makeQuery(id+"F12.opExtrude","SWEPT_FACE",FACE,{"disambiguationData":[OSD([sQuery(id+"F11.wireOp",EDGE,"E73")])]})]}),makeQuery(id+"F19.opExtrude","SWEPT_FACE",FACE,{"disambiguationData":[OSD([sQuery(id+"F18.wireOp",EDGE,"E80.left")])]}),makeQuery(id+"F19.opExtrude","SWEPT_FACE",FACE,{"disambiguationData":[OSD([sQuery(id+"F18.wireOp",EDGE,"E82.left")])]})]}),makeQuery(id+"F21.opExtrude","SWEPT_FACE",FACE,{"disambiguationData":[OSD([sQuery(id+"F20.wireOp",EDGE,"E85.left")])]})]});
            var Q9;
            Q9=makeQuery(id+"F21.boolean.opBoolean","COPY",EDGE,{"derivedFrom":makeQuery(id+"F21.opExtrude","CAP_EDGE",EDGE,{"disambiguationData":[OSD([sQuery(id+"F20.wireOp",EDGE,"E85.top")])],"isStart":true})});
            var Q10;
            Q10=makeQuery(id+"F21.boolean.opBoolean","COPY",EDGE,{"derivedFrom":makeQuery(id+"F21.opExtrude","CAP_EDGE",EDGE,{"disambiguationData":[OSD([sQuery(id+"F20.wireOp",EDGE,"E85.right")])],"isStart":true})});
            var Q11;
            Q11=makeQuery(id+"F21.boolean.opBoolean","COPY",EDGE,{"derivedFrom":makeQuery(id+"F21.opExtrude","CAP_EDGE",EDGE,{"disambiguationData":[OSD([sQuery(id+"F20.wireOp",EDGE,"E85.bottom")])],"isStart":true})});
            var Q12;
            Q12=makeQuery(id+"F21.boolean.opBoolean","COPY",EDGE,{"derivedFrom":makeQuery(id+"F21.opExtrude","CAP_EDGE",EDGE,{"disambiguationData":[OSD([sQuery(id+"F20.wireOp",EDGE,"E85.left")])],"isStart":true})});
            var Q13;
            Q13=makeQuery(id+"F21.boolean.opBoolean","COPY",EDGE,{"derivedFrom":makeQuery(id+"F21.opExtrude","CAP_EDGE",EDGE,{"disambiguationData":[OSD([sQuery(id+"F20.wireOp",EDGE,"E83.right")])],"isStart":true})});
            var Q14;
            {var subQ1=sQuery(id+"F11.wireOp",EDGE,"E70");var subQ17=sQuery(id+"F0.wireOp",EDGE,"E9");var subQ18=sQuery(id+"F0.wireOp",EDGE,"E8");var subQ27=sQuery(id+"F20.wireOp",EDGE,"E83.top");var subQ29=sQuery(id+"F24.wireOp",EDGE,"E93.0");Q14=makeQuery(id+"F25.boolean.opBoolean","SPLIT",EDGE,{"disambiguationData":[TD([makeQuery(id+"F25.opExtrude","SWEPT_FACE",FACE,{"disambiguationData":[OSD([subQ29])]})])],"derivedFrom":makeQuery(id+"F21.boolean.opBoolean","MERGE",EDGE,{"derivedFrom":[makeQuery(id+"F12.boolean.opBoolean","MERGE",EDGE,{"derivedFrom":[makeQuery(id+"F10.boolean.opBoolean","SPLIT",EDGE,{"disambiguationData":[TD([makeQuery(id+"F1.opExtrude","SWEPT_FACE",FACE,{"disambiguationData":[OSD([subQ18])]})])],"derivedFrom":makeQuery(id+"F1.opExtrude","CAP_EDGE",EDGE,{"disambiguationData":[OSD([subQ17])],"isStart":false})}),makeQuery(id+"F12.opExtrude","CAP_EDGE",EDGE,{"disambiguationData":[OSD([subQ1])],"isStart":true})]}),makeQuery(id+"F21.opExtrude","CAP_EDGE",EDGE,{"disambiguationData":[OSD([subQ27])],"isStart":true})]})});}
            var Q15;
            Q15=makeQuery(id+"F25.opExtrude","CAP_EDGE",EDGE,{"disambiguationData":[OSD([sQuery(id+"F24.wireOp",EDGE,"E93.0")])],"isStart":true});
            var Q16;
            Q16=makeQuery(id+"F25.boolean.opBoolean","MERGE",EDGE,{"derivedFrom":[makeQuery(id+"F21.boolean.opBoolean","COPY",EDGE,{"derivedFrom":makeQuery(id+"F21.opExtrude","CAP_EDGE",EDGE,{"disambiguationData":[OSD([sQuery(id+"F20.wireOp",EDGE,"E83.bottom")])],"isStart":true})}),makeQuery(id+"F25.opExtrude","CAP_EDGE",EDGE,{"disambiguationData":[OSD([sQuery(id+"F24.wireOp",EDGE,"E92.0")])],"isStart":true})]});
            chamfer(context, id + "F49", {"entities" : qUnion([Q0, Q1, Q2, Q3, Q4, Q5, Q6, Q7, Q8, Q9, Q10, Q11, Q12, Q13, Q14, Q15, Q16]), "width" : 1 * mm, "tangentPropagation" : true});
        }
        {
            var Q0;
            {var subQ0=sQuery(id+"F7.wireOp",EDGE,"E40");var subQ1=sQuery(id+"F7.wireOp",EDGE,"E39");var subQ2=sQuery(id+"F7.wireOp",EDGE,"E38");var subQ3=sQuery(id+"F7.wireOp",EDGE,"E37");var subQ4=sQuery(id+"F7.wireOp",EDGE,"E36");var subQ5=sQuery(id+"F7.wireOp",EDGE,"E35");var subQ6=sQuery(id+"F7.wireOp",EDGE,"E34");var subQ7=sQuery(id+"F7.wireOp",EDGE,"E33");var subQ8=sQuery(id+"F7.wireOp",EDGE,"E32");var subQ9=sQuery(id+"F7.wireOp",EDGE,"E31");var subQ10=sQuery(id+"F7.wireOp",EDGE,"E30");var subQ11=sQuery(id+"F7.wireOp",EDGE,"E29");var subQ12=sQuery(id+"F2.wireOp",EDGE,"E24.1");var subQ13=sQuery(id+"F2.wireOp",EDGE,"E24.0");var subQ14=sQuery(id+"F0.wireOp",EDGE,"E23");var subQ15=sQuery(id+"F0.wireOp",EDGE,"E22");var subQ16=sQuery(id+"F0.wireOp",EDGE,"E21");var subQ17=sQuery(id+"F0.wireOp",EDGE,"E20");var subQ18=sQuery(id+"F0.wireOp",EDGE,"E19");var subQ19=sQuery(id+"F0.wireOp",EDGE,"E18");var subQ20=sQuery(id+"F0.wireOp",EDGE,"E17");var subQ21=sQuery(id+"F0.wireOp",EDGE,"E16");var subQ22=sQuery(id+"F0.wireOp",EDGE,"E15");var subQ23=sQuery(id+"F0.wireOp",EDGE,"E14");var subQ24=sQuery(id+"F0.wireOp",EDGE,"E13");var subQ25=sQuery(id+"F0.wireOp",EDGE,"E12");var subQ26=sQuery(id+"F0.wireOp",EDGE,"E11");var subQ27=sQuery(id+"F0.wireOp",EDGE,"E10");var subQ28=sQuery(id+"F0.wireOp",EDGE,"E9");var subQ29=sQuery(id+"F0.wireOp",EDGE,"E8");Q0=makeQuery(id+"F37.boolean.opBoolean","INTERSECT",EDGE,{"derivedFrom":[makeQuery(id+"F31.boolean.opBoolean","MERGE",FACE,{"derivedFrom":[makeQuery(id+"F29.boolean.opBoolean","MERGE",FACE,{"derivedFrom":[makeQuery(id+"F28.boolean.opBoolean","MERGE",FACE,{"derivedFrom":[makeQuery(id+"F12.boolean.opBoolean","MERGE",FACE,{"derivedFrom":[makeQuery(id+"F8.boolean.opBoolean","MERGE",FACE,{"derivedFrom":[makeQuery(id+"F3.boolean.opBoolean","MERGE",FACE,{"derivedFrom":[makeQuery(id+"F1.opExtrude","CAP_FACE",FACE,{"disambiguationData":[OSD([subQ29,subQ28,subQ27,subQ26,subQ25,subQ24,subQ23,subQ22,subQ21,subQ20,subQ19,subQ18,subQ17,subQ16,subQ15,subQ14])],"isStart":true}),makeQuery(id+"F3.opExtrude","CAP_FACE",FACE,{"disambiguationData":[OSD([subQ13])],"isStart":true}),makeQuery(id+"F3.opExtrude","CAP_FACE",FACE,{"disambiguationData":[OSD([subQ12])],"isStart":true})]}),makeQuery(id+"F8.opExtrude","CAP_FACE",FACE,{"disambiguationData":[OSD([subQ11,subQ10,subQ9,subQ8,subQ7,subQ6])],"isStart":true}),makeQuery(id+"F8.opExtrude","CAP_FACE",FACE,{"disambiguationData":[OSD([subQ5,subQ4,subQ3,subQ2,subQ1,subQ0])],"isStart":true})]}),makeQuery(id+"F12.opExtrude","CAP_FACE",FACE,{"disambiguationData":[OSD([subQ29,subQ28,subQ27,subQ26,subQ25,subQ24,subQ23,subQ22,subQ21,subQ20,subQ19,subQ18,subQ17,subQ16,subQ15,subQ14,subQ13,subQ12,subQ11,subQ10,subQ9,subQ8,subQ7,subQ6,subQ5,subQ4,subQ3,subQ2,subQ1,subQ0])],"isStart":false})]}),makeQuery(id+"F28.opExtrude","CAP_FACE",FACE,{"disambiguationData":[OSD([subQ29,subQ28,subQ27,subQ26,subQ25,subQ24,subQ23,subQ22,subQ21,subQ20,subQ19,subQ18,subQ17,subQ16,subQ15,subQ14,subQ13,subQ12,subQ11,subQ10,subQ9,subQ8,subQ7,subQ6,subQ5,subQ4,subQ3,subQ2,subQ1,subQ0])],"isStart":false})]}),makeQuery(id+"F29.opExtrude","CAP_FACE",FACE,{"disambiguationData":[OSD([subQ29,subQ28,subQ27,subQ26,subQ25,subQ24,subQ23,subQ22,subQ21,subQ20,subQ19,subQ18,subQ17,subQ16,subQ15,subQ14,subQ13,subQ12,subQ11,subQ10,subQ9,subQ8,subQ7,subQ6,subQ5,subQ4,subQ3,subQ2,subQ1,subQ0])],"isStart":false})]}),makeQuery(id+"F31.opExtrude","CAP_FACE",FACE,{"disambiguationData":[OSD([sQuery(id+"F30.wireOp",EDGE,"E109"),sQuery(id+"F30.wireOp",EDGE,"E110"),sQuery(id+"F30.wireOp",EDGE,"E111"),sQuery(id+"F30.wireOp",EDGE,"E112"),sQuery(id+"F30.wireOp",EDGE,"E113"),sQuery(id+"F30.wireOp",EDGE,"E114"),sQuery(id+"F30.wireOp",EDGE,"E115"),sQuery(id+"F30.wireOp",EDGE,"E116")])],"isStart":true})]}),makeQuery(id+"F37.opExtrude","SWEPT_FACE",FACE,{"disambiguationData":[OSD([sQuery(id+"F36.wireOp",EDGE,"E130.right")])]})]});}
            var Q1;
            {var subQ0=sQuery(id+"F7.wireOp",EDGE,"E40");var subQ1=sQuery(id+"F7.wireOp",EDGE,"E39");var subQ2=sQuery(id+"F7.wireOp",EDGE,"E38");var subQ3=sQuery(id+"F7.wireOp",EDGE,"E37");var subQ4=sQuery(id+"F7.wireOp",EDGE,"E36");var subQ5=sQuery(id+"F7.wireOp",EDGE,"E35");var subQ6=sQuery(id+"F7.wireOp",EDGE,"E34");var subQ7=sQuery(id+"F7.wireOp",EDGE,"E33");var subQ8=sQuery(id+"F7.wireOp",EDGE,"E32");var subQ9=sQuery(id+"F7.wireOp",EDGE,"E31");var subQ10=sQuery(id+"F7.wireOp",EDGE,"E30");var subQ11=sQuery(id+"F7.wireOp",EDGE,"E29");var subQ12=sQuery(id+"F2.wireOp",EDGE,"E24.1");var subQ13=sQuery(id+"F2.wireOp",EDGE,"E24.0");var subQ14=sQuery(id+"F0.wireOp",EDGE,"E23");var subQ15=sQuery(id+"F0.wireOp",EDGE,"E22");var subQ16=sQuery(id+"F0.wireOp",EDGE,"E21");var subQ17=sQuery(id+"F0.wireOp",EDGE,"E20");var subQ18=sQuery(id+"F0.wireOp",EDGE,"E19");var subQ19=sQuery(id+"F0.wireOp",EDGE,"E18");var subQ20=sQuery(id+"F0.wireOp",EDGE,"E17");var subQ21=sQuery(id+"F0.wireOp",EDGE,"E16");var subQ22=sQuery(id+"F0.wireOp",EDGE,"E15");var subQ23=sQuery(id+"F0.wireOp",EDGE,"E14");var subQ24=sQuery(id+"F0.wireOp",EDGE,"E13");var subQ25=sQuery(id+"F0.wireOp",EDGE,"E12");var subQ26=sQuery(id+"F0.wireOp",EDGE,"E11");var subQ27=sQuery(id+"F0.wireOp",EDGE,"E10");var subQ28=sQuery(id+"F0.wireOp",EDGE,"E9");var subQ29=sQuery(id+"F0.wireOp",EDGE,"E8");Q1=makeQuery(id+"F37.boolean.opBoolean","INTERSECT",EDGE,{"derivedFrom":[makeQuery(id+"F31.boolean.opBoolean","MERGE",FACE,{"derivedFrom":[makeQuery(id+"F29.boolean.opBoolean","MERGE",FACE,{"derivedFrom":[makeQuery(id+"F28.boolean.opBoolean","MERGE",FACE,{"derivedFrom":[makeQuery(id+"F12.boolean.opBoolean","MERGE",FACE,{"derivedFrom":[makeQuery(id+"F8.boolean.opBoolean","MERGE",FACE,{"derivedFrom":[makeQuery(id+"F3.boolean.opBoolean","MERGE",FACE,{"derivedFrom":[makeQuery(id+"F1.opExtrude","CAP_FACE",FACE,{"disambiguationData":[OSD([subQ29,subQ28,subQ27,subQ26,subQ25,subQ24,subQ23,subQ22,subQ21,subQ20,subQ19,subQ18,subQ17,subQ16,subQ15,subQ14])],"isStart":true}),makeQuery(id+"F3.opExtrude","CAP_FACE",FACE,{"disambiguationData":[OSD([subQ13])],"isStart":true}),makeQuery(id+"F3.opExtrude","CAP_FACE",FACE,{"disambiguationData":[OSD([subQ12])],"isStart":true})]}),makeQuery(id+"F8.opExtrude","CAP_FACE",FACE,{"disambiguationData":[OSD([subQ11,subQ10,subQ9,subQ8,subQ7,subQ6])],"isStart":true}),makeQuery(id+"F8.opExtrude","CAP_FACE",FACE,{"disambiguationData":[OSD([subQ5,subQ4,subQ3,subQ2,subQ1,subQ0])],"isStart":true})]}),makeQuery(id+"F12.opExtrude","CAP_FACE",FACE,{"disambiguationData":[OSD([subQ29,subQ28,subQ27,subQ26,subQ25,subQ24,subQ23,subQ22,subQ21,subQ20,subQ19,subQ18,subQ17,subQ16,subQ15,subQ14,subQ13,subQ12,subQ11,subQ10,subQ9,subQ8,subQ7,subQ6,subQ5,subQ4,subQ3,subQ2,subQ1,subQ0])],"isStart":false})]}),makeQuery(id+"F28.opExtrude","CAP_FACE",FACE,{"disambiguationData":[OSD([subQ29,subQ28,subQ27,subQ26,subQ25,subQ24,subQ23,subQ22,subQ21,subQ20,subQ19,subQ18,subQ17,subQ16,subQ15,subQ14,subQ13,subQ12,subQ11,subQ10,subQ9,subQ8,subQ7,subQ6,subQ5,subQ4,subQ3,subQ2,subQ1,subQ0])],"isStart":false})]}),makeQuery(id+"F29.opExtrude","CAP_FACE",FACE,{"disambiguationData":[OSD([subQ29,subQ28,subQ27,subQ26,subQ25,subQ24,subQ23,subQ22,subQ21,subQ20,subQ19,subQ18,subQ17,subQ16,subQ15,subQ14,subQ13,subQ12,subQ11,subQ10,subQ9,subQ8,subQ7,subQ6,subQ5,subQ4,subQ3,subQ2,subQ1,subQ0])],"isStart":false})]}),makeQuery(id+"F31.opExtrude","CAP_FACE",FACE,{"disambiguationData":[OSD([sQuery(id+"F30.wireOp",EDGE,"E109"),sQuery(id+"F30.wireOp",EDGE,"E110"),sQuery(id+"F30.wireOp",EDGE,"E111"),sQuery(id+"F30.wireOp",EDGE,"E112"),sQuery(id+"F30.wireOp",EDGE,"E113"),sQuery(id+"F30.wireOp",EDGE,"E114"),sQuery(id+"F30.wireOp",EDGE,"E115"),sQuery(id+"F30.wireOp",EDGE,"E116")])],"isStart":true})]}),makeQuery(id+"F37.opExtrude","SWEPT_FACE",FACE,{"disambiguationData":[OSD([sQuery(id+"F36.wireOp",EDGE,"E129.right")])]})]});}
            chamfer(context, id + "F50", {"entities" : qUnion([Q0, Q1]), "width" : 1 * mm, "tangentPropagation" : true});
        }
    });
